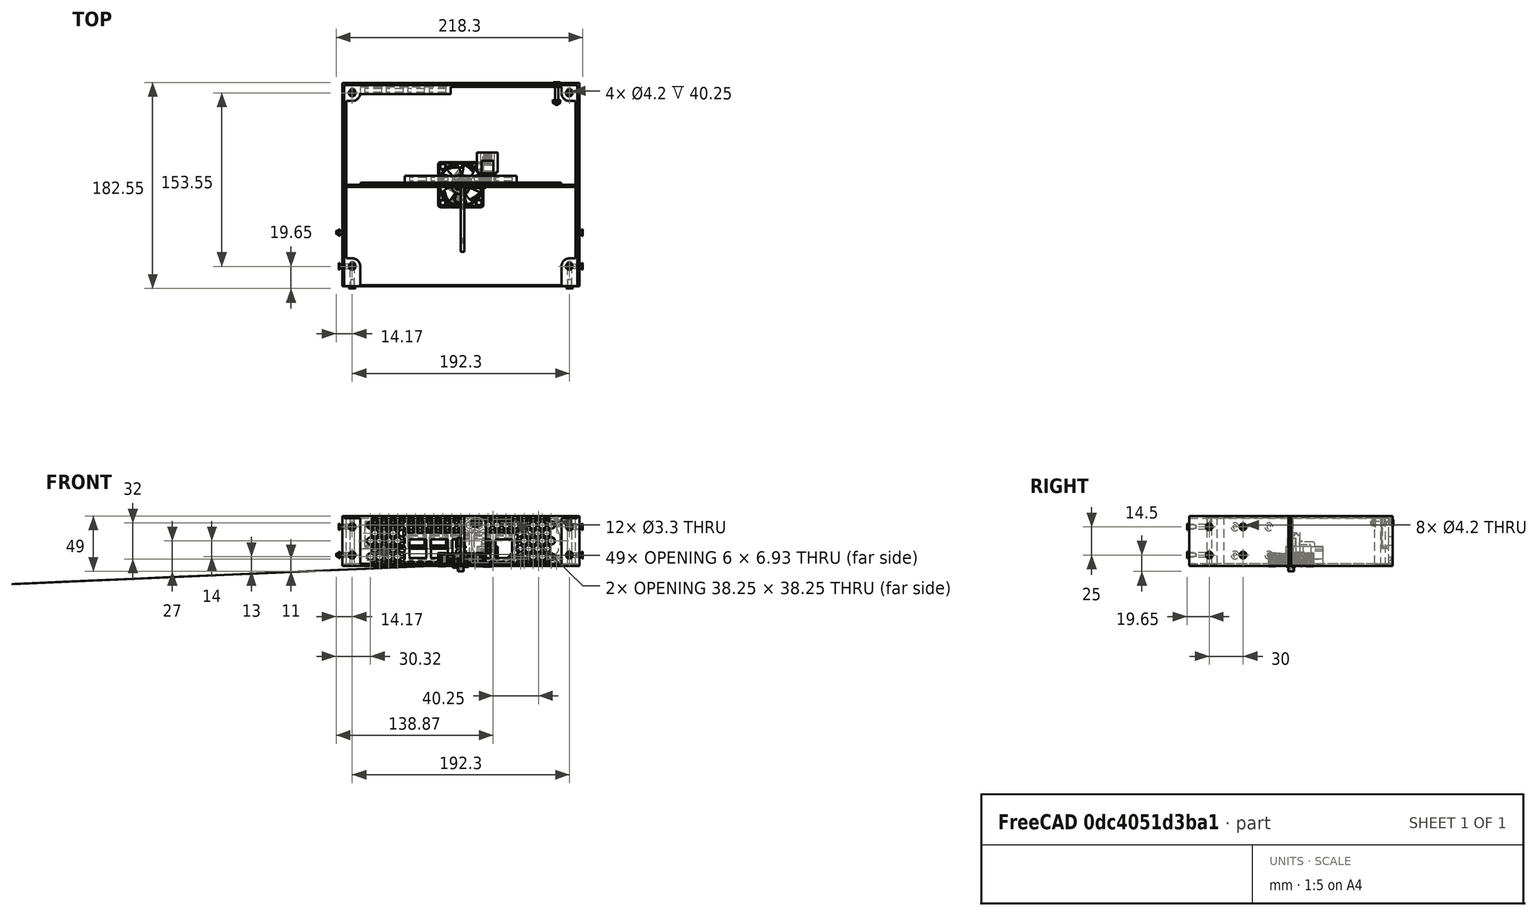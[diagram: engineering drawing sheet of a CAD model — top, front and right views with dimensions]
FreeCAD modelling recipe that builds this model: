
FCSTD DOCUMENT  (FreeCAD 1.1R20260108 (Git shallow))
Label: Rack box
License: All rights reserved
LicenseURL: https://en.wikipedia.org/wiki/All_rights_reserved
objects: Part::Feature×35, App::FeaturePython×25, Sketcher::SketchObject×22, Part::FeaturePython×19, App::Point×15, PartDesign::Pocket×12, PartDesign::Pad×10, App::Part×10, PartDesign::LinearPattern×7, PartDesign::Chamfer×6, App::Link×6, PartDesign::Body×4, PartDesign::MultiTransform×4, PartDesign::Mirrored×3, PartDesign::Fillet×2, Spreadsheet::Sheet×1, App::DocumentObjectGroup×1, PartDesign::Plane×1, Assembly::JointGroup×1, Assembly::AssemblyObject×1
note: 221 computed .brp shape members not serialized (recipe doc carries the construction recipe); baked Part::Feature solids carry a one-line shape summary decoded from their .brp

FEATURE [Spreadsheet::Sheet] Spreadsheet  label="Params"
  cells = A1='Box Length; B1(boxLength)=180; A2='Box Width; B2(boxWidth)=210; A3='Box Height; B3=1; C3='Constrained :; D3(boxHeight)==min(3; max(B3; 1)); A5='Rack ear depth; B5(rackEarDepth)=50; A6='Rack ear thickness; B6(rackEarThickness)=3; A7='Rack Unit; B7(rackUnit)=44.45; A8='Rack Unit Tolerance; B8(rackUnitTolerance)=0.45; A9='Rack Total Width; B9(rackTotalWidth)=254; A10='Rack Hole Spread; B10(rackHoleSpread)=236.525; A11='Rack Hole Spacing; B11(rackHoleSpacing)=15.875; C11='From center hole; A12='Rack hole Diameter; B12(rackHoleDiam)=6; A13='Wall Thickness; B13(wallThickness)=1.75; A14='Front thickness; B14(frontThickness)=2; A16='M3 heat set insert diam; B16(M3InsertDiam)=4.2; A17='Fit tolerance; B17(fitTol)=0.25; A18='M3 Screw hole; B18(M3ScrewHole)=3.3; A19='ISO 10642 Cone depth+tol; B19(iso10642coneDetph)=1.85; A20='Front Hole tp-bottom spacing; B20(frontHoleTopBottomSpace)=9.5; A22='Keystone Hole Width; B22(keystoneHoleWidth)=14.8; A23='Keystone Hole Height; B23(keystoneHoleHeight)=16.8; A24='Keystone Catch Height; B24(keystoneCatchHeight)=19.8; C24='From bottom of keystone; A25='Keystone Stop depth; B25(keystoneStopDepth)=9.75; A26='Keystone Catch Depth; B26(keystoneCatchDepth)=8.2; A27='Keystone Amount Front X; B27(keystoneFrontX)=5; A28='Keystone Amount Front Y; B28(keystoneFrontY)=1; A29='Keystone Amount Back X; B29(keystoneBackX)=4; A30='AndersonPowerpole Width; B30(andersonPowerpoleWidth)=16.75; A31='AndersonPowerpole Height; B31(andersonPowerpoleHeight)=8.75; A32='AndersonPowerpole Length; B32(andersonPowerpoleLength)=24.75; A35='Vent Hole Diam; B35(ventHoleDiam)=6; A36='Fan amount X; B36(fanAmountX)=2; C36='max 3; A37='Fan amout Y; B37(fanAmountY)=5; C37='max box height; A39='Rack Ear Thickness (3D printed); B39(rackEarThick3D)=3
FEATURE [App::DocumentObjectGroup] Measurements
FEATURE [Sketcher::SketchObject] Sketch011
  ArcFitTolerance = 1e-06
  AttachmentSupport = -> [YZ_Plane013]
  ExternalTypes = [0]
  FullyConstrained = true
  MakeInternals = false
  MapMode = 5
  Placement = pos=(0,0,0) rot=(0.57735,0.57735,0.57735;2.0944rad)
  expr: Constraints[14] = <<Params>>.M3ScrewHole
  expr: Constraints[28] = <<Params>>.boxHeight * <<Params>>.rackUnit - <<Params>>.rackUnitTolerance - 2 * <<Params>>.frontHoleTopBottomSpace
  expr: Constraints[30] = <<Params>>.frontThickness + 17.6
  expr: Constraints[32] = (<<Params>>.rackUnit * <<Params>>.boxHeight - <<Params>>.rackUnitTolerance) / 2
  expr: Constraints[33] = <<Params>>.rackUnit * <<Params>>.boxHeight - <<Params>>.rackUnitTolerance
  sketch-geometry (14):
    g0: LineSegment StartX=0 StartY=44 StartZ=0 EndX=-59.6 EndY=44 EndZ=0
    g1: LineSegment StartX=-59.6 StartY=44 StartZ=0 EndX=-59.6 EndY=0 EndZ=0
    g2: LineSegment StartX=-59.6 StartY=0 StartZ=0 EndX=0 EndY=0 EndZ=0
    g3: LineSegment StartX=0 StartY=0 StartZ=0 EndX=0 EndY=44 EndZ=0
    g4: LineSegment [constr] StartX=-49.6 StartY=9.5 StartZ=0 EndX=-49.6 EndY=0 EndZ=0
    g5: Circle CenterX=-49.6 CenterY=34.5 CenterZ=0 NormalX=0 NormalY=0 NormalZ=1 AngleXU=0 Radius=1.65
    g6: Circle CenterX=-19.6 CenterY=34.5 CenterZ=0 NormalX=0 NormalY=0 NormalZ=1 AngleXU=0 Radius=1.65
    g7: Circle CenterX=-49.6 CenterY=9.5 CenterZ=0 NormalX=0 NormalY=0 NormalZ=1 AngleXU=0 Radius=1.65
    g8: Circle CenterX=-19.6 CenterY=9.5 CenterZ=0 NormalX=0 NormalY=0 NormalZ=1 AngleXU=0 Radius=1.65
    g9: LineSegment [constr] StartX=-49.6 StartY=34.5 StartZ=0 EndX=-19.6 EndY=34.5 EndZ=0
    g10: LineSegment [constr] StartX=-19.6 StartY=34.5 StartZ=0 EndX=-19.6 EndY=9.5 EndZ=0
    g11: LineSegment [constr] StartX=-19.6 StartY=9.5 StartZ=0 EndX=-49.6 EndY=9.5 EndZ=0
    g12: LineSegment [constr] StartX=-49.6 StartY=9.5 StartZ=0 EndX=-49.6 EndY=34.5 EndZ=0
    g13: GeomPoint [constr] X=-19.6 Y=22 Z=0
  constraints (36):
    c: Coincident(g0,g1)
    c: Coincident(g1,g2)
    c: Coincident(g2,g3)
    c: Coincident(g3,g0)
    c: Horizontal(g0)
    c: Horizontal(g2)
    c: Vertical(g1)
    c: Vertical(g3)
    c: PointOnObject(g4,g2)
    c: Vertical(g4)
    c: Coincident(g7,g4)
    c: Equal(g7,g5)
    c: Equal(g5,g6)
    c: Equal(g6,g8)
    c: Diameter(g7) = 3.3
    c: Coincident(g9,g5)
    c: Coincident(g9,g6)
    c: Horizontal(g9)
    c: Coincident(g10,g6)
    c: Coincident(g10,g8)
    c: Vertical(g10)
    c: Coincident(g11,g8)
    c: Coincident(g11,g4)
    c: Horizontal(g11)
    c: Coincident(g12,g4)
    c: Coincident(g12,g5)
    c: Vertical(g12)
    c: DistanceX(g9,g9) = 30
    c: DistanceY(g10,g10) = 25
    c: PointOnObject(g-1,g2)
    c: DistanceX(g8,g2) = 19.6
    c: Symmetric(g10,g10,g13)
    c: DistanceY(g-1,g13) = 22
    c: DistanceY(g3,g3) = 44
    c: PointOnObject(g-1,g3)
    c: DistanceX(g1,g8) = 40
FEATURE [PartDesign::Pad] Pad006
  Direction = (1,0,0)
  Length = 3
  Length2 = 10
  Placement = pos=(0,0,0) rot=(1,1,1;2.0944rad)
  Profile = -> Sketch011
  ReferenceAxis = -> Sketch011 [N_Axis]
  Refine = true
  SideType = 0
  Suppressed = false
  Type = 0
  Type2 = 0
  expr: Length = <<Params>>.rackEarThick3D
FEATURE [PartDesign::Chamfer] Chamfer003
  Angle = 45
  Base = -> Pad006 [Edge15,Edge18,Edge21,Edge24]
  BaseFeature = -> Pad006
  ChamferType = 0
  FlipDirection = false
  Placement = pos=(0,0,0) rot=(1,1,1;2.0944rad)
  Refine = true
  Size = 1.85
  Size2 = 1
  SupportTransform = false
  Suppressed = false
  UseAllEdges = false
  expr: Size = min(<<Params>>.iso10642coneDetph; <<Params>>.rackEarThick3D - 0.01)
FEATURE [Sketcher::SketchObject] Sketch012
  ArcFitTolerance = 1e-06
  AttachmentSupport = -> [Chamfer003]
  ExternalGeometry = -> [Chamfer003]
  ExternalTypes = [0]
  FullyConstrained = true
  MakeInternals = false
  MapMode = 5
  Placement = pos=(3,-7e-16,3e-16) rot=(0.57735,0.57735,0.57735;2.0944rad)
  expr: Constraints[10] = <<Params>>.rackEarThick3D
  sketch-geometry (4):
    g0: LineSegment StartX=3.6e-15 StartY=44 StartZ=0 EndX=-3 EndY=44 EndZ=0
    g1: LineSegment StartX=-3 StartY=44 StartZ=0 EndX=-3 EndY=0 EndZ=0
    g2: LineSegment StartX=-3 StartY=0 StartZ=0 EndX=3.6e-15 EndY=0 EndZ=0
    g3: LineSegment StartX=3.6e-15 StartY=0 StartZ=0 EndX=3.6e-15 EndY=44 EndZ=0
  constraints (11):
    c: Coincident(g0,g1)
    c: Coincident(g1,g2)
    c: Coincident(g2,g3)
    c: Coincident(g3,g0)
    c: Horizontal(g0)
    c: Horizontal(g2)
    c: Vertical(g1)
    c: Vertical(g3)
    c: Coincident(g0,g-3)
    c: PointOnObject(g-3,g2)
    c: DistanceX(g0,g0) = 3
FEATURE [PartDesign::Pad] Pad007
  BaseFeature = -> Chamfer003
  Direction = (1,0,0)
  Length = 19
  Length2 = 10
  Placement = pos=(0,0,0) rot=(1,1,1;2.0944rad)
  Profile = -> Sketch012
  ReferenceAxis = -> Sketch012 [N_Axis]
  Refine = true
  SideType = 0
  Suppressed = false
  Type = 0
  Type2 = 0
  expr: Length = (<<Params>>.rackTotalWidth - <<Params>>.boxWidth) / 2 - <<Params>>.rackEarThick3D
FEATURE [Sketcher::SketchObject] Sketch
  ArcFitTolerance = 1e-06
  AttachmentSupport = -> [XY_Plane002]
  ExternalTypes = [0]
  FullyConstrained = true
  MakeInternals = false
  MapMode = 2
  expr: Constraints[10] = <<Params>>.boxWidth
  expr: Constraints[11] = <<Params>>.boxLength
  sketch-geometry (5):
    g0: LineSegment StartX=-105 StartY=90 StartZ=0 EndX=-105 EndY=-90 EndZ=0
    g1: LineSegment StartX=-105 StartY=-90 StartZ=0 EndX=105 EndY=-90 EndZ=0
    g2: LineSegment StartX=105 StartY=-90 StartZ=0 EndX=105 EndY=90 EndZ=0
    g3: LineSegment StartX=105 StartY=90 StartZ=0 EndX=-105 EndY=90 EndZ=0
    g4: GeomPoint [constr] X=2e-16 Y=-2e-16 Z=0
  constraints (12):
    c: Coincident(g0,g1)
    c: Coincident(g1,g2)
    c: Coincident(g2,g3)
    c: Coincident(g3,g0)
    c: Vertical(g0)
    c: Vertical(g2)
    c: Horizontal(g1)
    c: Horizontal(g3)
    c: Symmetric(g2,g0,g4)
    c: Coincident(g4,g-1)
    c: DistanceX(g3,g3) = 210
    c: DistanceY(g2,g2) = 180
FEATURE [PartDesign::Pad] Pad  label="PROBLEMATIC_PAD"
  Direction = (0,0,1)
  Length = 44
  Length2 = 10
  Profile = -> Sketch
  ReferenceAxis = -> Sketch [N_Axis]
  Refine = true
  SideType = 0
  Suppressed = false
  Type = 0
  Type2 = 0
  expr: Length = <<Params>>.boxHeight * <<Params>>.rackUnit - <<Params>>.rackUnitTolerance
FEATURE [Sketcher::SketchObject] Sketch001
  ArcFitTolerance = 1e-06
  AttachmentSupport = -> [Pad]
  ExternalTypes = [0]
  FullyConstrained = true
  MakeInternals = false
  MapMode = 5
  Placement = pos=(0,0,44) rot=(0,0,1;0rad)
  expr: Constraints[10] = <<Params>>.boxWidth - 2 * <<Params>>.wallThickness
  expr: Constraints[11] = <<Params>>.boxLength - <<Params>>.wallThickness
  expr: Constraints[12] = <<Params>>.boxLength / 2 - <<Params>>.wallThickness
  sketch-geometry (5):
    g0: LineSegment StartX=-103.25 StartY=-90 StartZ=0 EndX=103.25 EndY=-90 EndZ=0
    g1: LineSegment StartX=103.25 StartY=-90 StartZ=0 EndX=103.25 EndY=88.25 EndZ=0
    g2: LineSegment StartX=103.25 StartY=88.25 StartZ=0 EndX=-103.25 EndY=88.25 EndZ=0
    g3: LineSegment StartX=-103.25 StartY=88.25 StartZ=0 EndX=-103.25 EndY=-90 EndZ=0
    g4: GeomPoint X=0 Y=-90 Z=0
  constraints (13):
    c: Coincident(g0,g1)
    c: Coincident(g1,g2)
    c: Coincident(g2,g3)
    c: Coincident(g3,g0)
    c: Horizontal(g0)
    c: Horizontal(g2)
    c: Vertical(g1)
    c: Vertical(g3)
    c: Symmetric(g0,g0,g4)
    c: PointOnObject(g4,g-2)
    c: DistanceX(g2,g2) = 206.5
    c: DistanceY(g3,g3) = 178.25
    c: DistanceY(g-1,g2) = 88.25
FEATURE [PartDesign::Pocket] Pocket
  BaseFeature = -> Pad
  Direction = (0,0,-1)
  Length = 0
  Length2 = 5
  Offset = -1.75
  Profile = -> Sketch001
  ReferenceAxis = -> Sketch001 [N_Axis]
  Refine = true
  SideType = 0
  Suppressed = false
  Type = 3
  Type2 = 0
  UpToFace = -> Pad [Face5]
  expr: Offset = -<<Params>>.wallThickness
FEATURE [Sketcher::SketchObject] Sketch002
  ArcFitTolerance = 1e-06
  AttachmentSupport = -> [Pocket]
  ExternalTypes = [0]
  FullyConstrained = true
  MakeInternals = false
  MapMode = 5
  Placement = pos=(0,0,1.75) rot=(0,0,1;0rad)
  expr: Constraints[0] = <<Params>>.M3InsertDiam
  expr: Constraints[23] = <<Params>>.boxWidth / 2 - <<Params>>.wallThickness
  expr: Constraints[25] = 17.6 mm
  expr: Constraints[26] = <<Params>>.boxLength / 2
  expr: Constraints[31] = <<Params>>.boxLength - <<Params>>.wallThickness
  expr: Constraints[36] = <<Params>>.wallThickness
  expr: Constraints[65] = <<Params>>.wallThickness
  sketch-geometry (27):
    g0: Circle CenterX=-96.15 CenterY=81.15 CenterZ=0 NormalX=0 NormalY=0 NormalZ=1 AngleXU=0 Radius=2.1
    g1: LineSegment StartX=-89.05 StartY=-90 StartZ=0 EndX=-89.05 EndY=-72.4 EndZ=0
    g2: Circle CenterX=-96.15 CenterY=-72.4 CenterZ=0 NormalX=0 NormalY=0 NormalZ=1 AngleXU=0 Radius=2.1
    g3: ArcOfCircle CenterX=-96.15 CenterY=81.15 CenterZ=0 NormalX=0 NormalY=0 NormalZ=1 AngleXU=0 Radius=7.1 StartAngle=4.71239 EndAngle=6.28319
    g4: ArcOfCircle CenterX=-96.15 CenterY=-72.4 CenterZ=0 NormalX=0 NormalY=0 NormalZ=1 AngleXU=0 Radius=7.1 StartAngle=2e-16 EndAngle=1.5708
    g5: LineSegment [constr] StartX=-96.15 StartY=81.15 StartZ=0 EndX=-96.15 EndY=-72.4 EndZ=0
    g6: LineSegment StartX=-89.05 StartY=-90 StartZ=0 EndX=-103.25 EndY=-90 EndZ=0
    g7: LineSegment StartX=-101.5 StartY=74.05 StartZ=0 EndX=-101.5 EndY=-65.3 EndZ=0
    g8: LineSegment StartX=-96.15 StartY=74.05 StartZ=0 EndX=-101.5 EndY=74.05 EndZ=0
    g9: LineSegment StartX=-101.5 StartY=-65.3 StartZ=0 EndX=-96.15 EndY=-65.3 EndZ=0
    g10: LineSegment StartX=-103.25 StartY=-90 StartZ=0 EndX=-103.25 EndY=88.25 EndZ=0
    g11: LineSegment StartX=-89.05 StartY=86.5 StartZ=0 EndX=0 EndY=86.5 EndZ=0
    g12: LineSegment StartX=-89.05 StartY=81.15 StartZ=0 EndX=-89.05 EndY=86.5 EndZ=0
    g13: LineSegment StartX=-103.25 StartY=88.25 StartZ=0 EndX=0 EndY=88.25 EndZ=0
    g14: LineSegment StartX=103.25 StartY=88.25 StartZ=0 EndX=0 EndY=88.25 EndZ=0
    g15: LineSegment StartX=89.05 StartY=86.5 StartZ=0 EndX=0 EndY=86.5 EndZ=0
    g16: LineSegment StartX=89.05 StartY=81.15 StartZ=0 EndX=89.05 EndY=86.5 EndZ=0
    g17: ArcOfCircle CenterX=96.15 CenterY=81.15 CenterZ=0 NormalX=0 NormalY=0 NormalZ=1 AngleXU=0 Radius=7.1 StartAngle=3.14159 EndAngle=4.71239
    g18: LineSegment StartX=96.15 StartY=74.05 StartZ=0 EndX=101.5 EndY=74.05 EndZ=0
    g19: LineSegment StartX=103.25 StartY=-90 StartZ=0 EndX=103.25 EndY=88.25 EndZ=0
    g20: Circle CenterX=96.15 CenterY=81.15 CenterZ=0 NormalX=0 NormalY=0 NormalZ=1 AngleXU=0 Radius=2.1
    g21: ArcOfCircle CenterX=96.15 CenterY=-72.4 CenterZ=0 NormalX=0 NormalY=0 NormalZ=1 AngleXU=0 Radius=7.1 StartAngle=1.5708 EndAngle=3.14159
    g22: LineSegment StartX=89.05 StartY=-90 StartZ=0 EndX=89.05 EndY=-72.4 EndZ=0
    g23: LineSegment StartX=89.05 StartY=-90 StartZ=0 EndX=103.25 EndY=-90 EndZ=0
    g24: LineSegment StartX=101.5 StartY=-65.3 StartZ=0 EndX=96.15 EndY=-65.3 EndZ=0
    g25: LineSegment StartX=101.5 StartY=74.05 StartZ=0 EndX=101.5 EndY=-65.3 EndZ=0
    g26: Circle CenterX=96.15 CenterY=-72.4 CenterZ=0 NormalX=0 NormalY=0 NormalZ=1 AngleXU=0 Radius=2.1
  constraints (66):
    c: Diameter(g0) = 4.2
    c: Vertical(g1)
    c: Equal(g0,g2)
    c: Coincident(g3,g0)
    c: Coincident(g4,g2)
    c: Tangent(g4,g1) = -1.5708
    c: Coincident(g5,g0)
    c: Coincident(g5,g2)
    c: Vertical(g5)
    c: Distance(g2,g1) = 5
    c: Coincident(g6,g1)
    c: Vertical(g7)
    c: Coincident(g8,g7)
    c: Horizontal(g8)
    c: Tangent(g8,g3) = 1.5708
    c: Coincident(g9,g7)
    c: Horizontal(g9)
    c: Tangent(g9,g4) = 1.5708
    c: Coincident(g10,g6)
    c: Distance(g0,g10) = 5
    c: Distance(g3,g0) = 5
    c: Horizontal(g11)
    c: Coincident(g12,g11)
    c: DistanceX(g6,g-1) = 103.25
    c: Vertical(g10)
    c: DistanceY(g6,g2) = 17.6
    c: DistanceY(g6,g-1) = 90
    c: Horizontal(g6)
    c: PointOnObject(g11,g-2)
    c: Tangent(g12,g3) = -1.5708
    c: Vertical(g12)
    c: DistanceY(g10,g10) = 178.25
    c: Equal(g8,g12)
    c: Coincident(g13,g10)
    c: PointOnObject(g13,g-2)
    c: Horizontal(g13)
    c: Distance(g11,g13) = 1.75
    c: Equal(g0,g20)
    c: Symmetric(g0,g20,g-2)
    c: Symmetric(g1,g22,g-2)
    c: Symmetric(g1,g22,g-2)
    c: Equal(g3,g17)
    c: Symmetric(g3,g17,g-2)
    c: Symmetric(g3,g17,g-2)
    c: Equal(g4,g21)
    c: Symmetric(g4,g21,g-2)
    c: Symmetric(g4,g21,g-2)
    c: Symmetric(g6,g23,g-2)
    c: Symmetric(g6,g23,g-2)
    c: Symmetric(g7,g25,g-2)
    c: Symmetric(g7,g25,g-2)
    c: Symmetric(g8,g18,g-2)
    c: Symmetric(g8,g18,g-2)
    c: Symmetric(g9,g24,g-2)
    c: Symmetric(g9,g24,g-2)
    c: Symmetric(g10,g19,g-2)
    c: Symmetric(g10,g19,g-2)
    c: Symmetric(g11,g15,g-2)
    c: Symmetric(g12,g16,g-2)
    c: Symmetric(g12,g16,g-2)
    c: Symmetric(g13,g14,g-2)
    c: Coincident(g15,g11)
    c: Coincident(g14,g13)
    c: Equal(g2,g26)
    c: Symmetric(g2,g26,g-2)
    c: DistanceX(g10,g7) = 1.75
FEATURE [PartDesign::Pad] Pad001
  BaseFeature = -> Pocket
  Direction = (0,0,1)
  Length = 10
  Length2 = 10
  Offset = 2
  Profile = -> Sketch002
  ReferenceAxis = -> Sketch002 [N_Axis]
  Refine = true
  SideType = 0
  Suppressed = false
  Type = 3
  Type2 = 0
  UpToFace = -> Pocket [Face5]
  expr: Offset = <<Params>>.wallThickness + <<Params>>.fitTol
FEATURE [Sketcher::SketchObject] Sketch003
  ArcFitTolerance = 1e-06
  AttachmentSupport = -> [Pad001]
  ExternalTypes = [0]
  FullyConstrained = true
  MakeInternals = false
  MapMode = 5
  Placement = pos=(0,-90,0) rot=(1,0,0;1.5708rad)
  expr: .Constraints.frontHole = <<Params>>.M3InsertDiam
  expr: Constraints[10] = <<Params>>.rackUnit * <<Params>>.boxHeight - <<Params>>.rackUnitTolerance
  expr: Constraints[11] = <<Params>>.boxWidth / 2 - (<<Params>>.wallThickness + 5 + <<Params>>.M3InsertDiam / 2)
  expr: Constraints[9] = <<Params>>.boxHeight * <<Params>>.rackUnit - <<Params>>.rackUnitTolerance - 2 * <<Params>>.frontHoleTopBottomSpace
  sketch-geometry (9):
    g0: LineSegment [constr] StartX=-96.15 StartY=44 StartZ=0 EndX=-96.15 EndY=0 EndZ=0
    g1: GeomPoint [constr] X=-96.15 Y=22 Z=0
    g2: Circle CenterX=-96.15 CenterY=34.5 CenterZ=0 NormalX=0 NormalY=0 NormalZ=1 AngleXU=0 Radius=2.1
    g3: Circle CenterX=-96.15 CenterY=9.5 CenterZ=0 NormalX=0 NormalY=0 NormalZ=1 AngleXU=0 Radius=2.1
    g4: Circle CenterX=96.15 CenterY=34.5 CenterZ=0 NormalX=0 NormalY=0 NormalZ=1 AngleXU=0 Radius=2.1
    g5: Circle CenterX=96.15 CenterY=9.5 CenterZ=0 NormalX=0 NormalY=0 NormalZ=1 AngleXU=0 Radius=2.1
    g6: LineSegment [constr] StartX=-96.15 StartY=0 StartZ=0 EndX=0 EndY=0 EndZ=0
    g7: LineSegment [constr] StartX=-96.15 StartY=34.5 StartZ=0 EndX=-96.15 EndY=9.5 EndZ=0
    g8: GeomPoint [constr] X=-96.15 Y=22 Z=0
  constraints (19):
    c: Vertical(g0)
    c: Symmetric(g0,g0,g1)
    c: PointOnObject(g2,g0)
    c: Diameter(g2) = 4.2  'frontHole'
    c: Equal(g3,g2)
    c: Equal(g2,g4)
    c: Symmetric(g2,g4,g-2)
    c: Equal(g3,g5)
    c: Symmetric(g3,g5,g-2)
    c: DistanceY(g3,g2) = 25
    c: DistanceY(g-1,g0) = 44
    c: DistanceX(g0,g-1) = 96.15
    c: Coincident(g6,g0)
    c: Coincident(g6,g-1)
    c: Horizontal(g6)
    c: Coincident(g7,g2)
    c: Coincident(g7,g3)
    c: Symmetric(g7,g7,g8)
    c: Coincident(g8,g1)
FEATURE [PartDesign::Pocket] Pocket001
  BaseFeature = -> Pad001
  Direction = (0,1,-2e-16)
  Length = 17.6
  Length2 = 5
  Offset = 2.1
  Profile = -> Sketch003
  ReferenceAxis = -> Sketch003 [N_Axis]
  Refine = true
  SideType = 0
  Suppressed = false
  Type = 0
  Type2 = 0
  UpToShape = -> [Pad001]
  expr: Length = 17.6
  expr: Offset = <<Params>>.M3InsertDiam / 2
FEATURE [Sketcher::SketchObject] Sketch010
  ArcFitTolerance = 1e-06
  AttachmentSupport = -> [Pocket001]
  ExternalTypes = [0]
  FullyConstrained = true
  MakeInternals = false
  MapMode = 5
  Placement = pos=(-105,0,0) rot=(0.57735,-0.57735,-0.57735;2.0944rad)
  expr: Constraints[15] = <<Params>>.M3InsertDiam
  expr: Constraints[17] = <<Params>>.rackUnit * <<Params>>.boxHeight - <<Params>>.rackUnitTolerance - 2 * <<Params>>.frontHoleTopBottomSpace
  expr: Constraints[20] = (<<Params>>.rackUnit * <<Params>>.boxHeight - <<Params>>.rackUnitTolerance) / 2
  expr: Constraints[21] = <<Params>>.boxLength / 2 - 17.6
  sketch-geometry (9):
    g0: LineSegment [constr] StartX=72.4 StartY=34.5 StartZ=0 EndX=42.4 EndY=34.5 EndZ=0
    g1: LineSegment [constr] StartX=42.4 StartY=34.5 StartZ=0 EndX=42.4 EndY=9.5 EndZ=0
    g2: LineSegment [constr] StartX=42.4 StartY=9.5 StartZ=0 EndX=72.4 EndY=9.5 EndZ=0
    g3: LineSegment [constr] StartX=72.4 StartY=9.5 StartZ=0 EndX=72.4 EndY=34.5 EndZ=0
    g4: Circle CenterX=42.4 CenterY=9.5 CenterZ=0 NormalX=0 NormalY=0 NormalZ=1 AngleXU=0 Radius=2.1
    g5: Circle CenterX=72.4 CenterY=9.5 CenterZ=0 NormalX=0 NormalY=0 NormalZ=1 AngleXU=0 Radius=2.1
    g6: Circle CenterX=42.4 CenterY=34.5 CenterZ=0 NormalX=0 NormalY=0 NormalZ=1 AngleXU=0 Radius=2.1
    g7: Circle CenterX=72.4 CenterY=34.5 CenterZ=0 NormalX=0 NormalY=0 NormalZ=1 AngleXU=0 Radius=2.1
    g8: GeomPoint [constr] X=72.4 Y=22 Z=0
  constraints (22):
    c: Coincident(g0,g1)
    c: Coincident(g1,g2)
    c: Coincident(g2,g3)
    c: Coincident(g3,g0)
    c: Horizontal(g0)
    c: Horizontal(g2)
    c: Vertical(g1)
    c: Vertical(g3)
    c: PointOnObject(g5,g2)
    c: DistanceX(g2,g2) = 30
    c: Coincident(g4,g1)
    c: Coincident(g6,g0)
    c: Equal(g7,g6)
    c: Equal(g6,g4)
    c: Equal(g4,g5)
    c: Diameter(g4) = 4.2
    c: Coincident(g0,g7)
    c: DistanceY(g1,g1) = 25
    c: PointOnObject(g5,g3)
    c: Symmetric(g3,g3,g8)
    c: DistanceY(g-1,g8) = 22
    c: DistanceX(g-1,g5) = 72.4
FEATURE [PartDesign::Pocket] Pocket004
  BaseFeature = -> Pocket001
  Direction = (1,0,0)
  Length = 0
  Length2 = 5
  Offset = 7.1
  Profile = -> Sketch010
  ReferenceAxis = -> Sketch010 [N_Axis]
  Refine = true
  SideType = 0
  Suppressed = false
  Type = 3
  Type2 = 0
  UpToFace = -> Pocket001 [Face3]
  expr: Offset = <<Params>>.M3InsertDiam / 2 + 5
FEATURE [PartDesign::Mirrored] Mirrored002
  BaseFeature = -> Pocket004
  MirrorPlane = -> YZ_Plane002
  Originals = -> [Pocket004]
  Refine = true
  Suppressed = false
  TransformMode = 0
FEATURE [Sketcher::SketchObject] Sketch013
  ArcFitTolerance = 1e-06
  AttachmentSupport = -> [Pad007]
  ExternalTypes = [0]
  FullyConstrained = true
  MakeInternals = false
  MapMode = 5
  Placement = pos=(0,3e-16,0) rot=(0.57735,0.57735,0.57735;4.18879rad)
  expr: Constraints[0] = <<Params>>.rackHoleDiam
  expr: Constraints[18] = <<Params>>.rackHoleDiam / 2 + <<Params>>.fitTol
  expr: Constraints[1] = <<Params>>.boxHeight > 1 ? <<Params>>.rackUnit * <<Params>>.boxHeight - (<<Params>>.rackUnit - <<Params>>.rackUnitTolerance) : <<Params>>.rackHoleSpacing * 2
  expr: Constraints[6] = <<Params>>.boxHeight > 1 ? <<Params>>.rackUnit / 2 - <<Params>>.rackUnitTolerance / 2 : <<Params>>.rackUnit / 2 - <<Params>>.rackUnitTolerance / 2 - <<Params>>.rackHoleSpacing
  expr: Constraints[7] = (<<Params>>.rackHoleSpread - <<Params>>.boxWidth) / 2
  sketch-geometry (13):
    g0: Circle [constr] CenterX=37.875 CenterY=13.2625 CenterZ=0 NormalX=0 NormalY=0 NormalZ=1 AngleXU=0 Radius=3
    g1: LineSegment [constr] StartX=37.875 StartY=13.2625 StartZ=0 EndX=6.125 EndY=13.2625 EndZ=0
    g2: Circle [constr] CenterX=6.125 CenterY=13.2625 CenterZ=0 NormalX=0 NormalY=0 NormalZ=1 AngleXU=0 Radius=3
    g3: ArcOfCircle CenterX=6.125 CenterY=14.7625 CenterZ=0 NormalX=0 NormalY=0 NormalZ=1 AngleXU=0 Radius=3.25 StartAngle=2e-16 EndAngle=3.14159
    g4: ArcOfCircle CenterX=6.125 CenterY=11.7625 CenterZ=0 NormalX=0 NormalY=0 NormalZ=1 AngleXU=0 Radius=3.25 StartAngle=3.14159 EndAngle=6.28319
    g5: LineSegment StartX=9.375 StartY=14.7625 StartZ=0 EndX=9.375 EndY=11.7625 EndZ=0
    g6: LineSegment StartX=2.875 StartY=14.7625 StartZ=0 EndX=2.875 EndY=11.7625 EndZ=0
    g7: LineSegment [constr] StartX=6.125 StartY=14.7625 StartZ=0 EndX=6.125 EndY=11.7625 EndZ=0
    g8: ArcOfCircle CenterX=37.875 CenterY=14.7625 CenterZ=0 NormalX=0 NormalY=0 NormalZ=1 AngleXU=0 Radius=3.25 StartAngle=2e-16 EndAngle=3.14159
    g9: ArcOfCircle CenterX=37.875 CenterY=11.7625 CenterZ=0 NormalX=0 NormalY=0 NormalZ=1 AngleXU=0 Radius=3.25 StartAngle=3.14159 EndAngle=6.28319
    g10: LineSegment StartX=41.125 StartY=14.7625 StartZ=0 EndX=41.125 EndY=11.7625 EndZ=0
    g11: LineSegment StartX=34.625 StartY=14.7625 StartZ=0 EndX=34.625 EndY=11.7625 EndZ=0
    g12: LineSegment [constr] StartX=37.875 StartY=14.7625 StartZ=0 EndX=37.875 EndY=11.7625 EndZ=0
  constraints (30):
    c: Diameter(g0) = 6
    c: Distance(g1,g1) = 31.75
    c: Coincident(g2,g1)
    c: Equal(g2,g0)
    c: Coincident(g1,g0)
    c: Horizontal(g1)
    c: DistanceX(g-1,g1) = 6.125
    c: Distance(g1,g-1) = 13.2625
    c: Tangent(g3,g5) = 1.5708
    c: Tangent(g3,g6) = -1.5708
    c: Tangent(g4,g5) = 1.5708
    c: Tangent(g4,g6) = -1.5708
    c: Equal(g3,g4)
    c: Coincident(g7,g3)
    c: Coincident(g7,g4)
    c: Symmetric(g7,g7,g1)
    c: Vertical(g7)
    c: DistanceY(g4,g3) = 3
    c: Radius(g3) = 3.25
    c: Tangent(g8,g10) = 1.5708
    c: Tangent(g8,g11) = -1.5708
    c: Tangent(g9,g10) = 1.5708
    c: Tangent(g9,g11) = -1.5708
    c: Equal(g8,g9)
    c: Coincident(g12,g8)
    c: Coincident(g12,g9)
    c: Symmetric(g12,g12,g0)
    c: Vertical(g12)
    c: Equal(g8,g3)
    c: Equal(g5,g11)
FEATURE [PartDesign::Pocket] Pocket005
  BaseFeature = -> Pad007
  Direction = (0,-1,0)
  Length = 5
  Length2 = 5
  Placement = pos=(0,0,0) rot=(1,1,1;2.0944rad)
  Profile = -> Sketch013
  ReferenceAxis = -> Sketch013 [N_Axis]
  Refine = true
  SideType = 0
  Suppressed = false
  Type = 1
  Type2 = 0
FEATURE [PartDesign::Fillet] Fillet
  Base = -> Pocket005 [Edge13]
  BaseFeature = -> Pocket005
  Placement = pos=(0,0,0) rot=(1,1,1;2.0944rad)
  Radius = 1.5
  Refine = true
  SupportTransform = false
  Suppressed = false
  UseAllEdges = false
FEATURE [Sketcher::SketchObject] Sketch014
  ArcFitTolerance = 1e-06
  AttachmentSupport = -> [Pocket001]
  ExternalTypes = [0]
  FullyConstrained = true
  MakeInternals = false
  MapMode = 5
  Placement = pos=(0,86.5,0) rot=(1,0,0;1.5708rad)
  expr: Constraints[19] = <<Params>>.M3ScrewHole
  expr: Constraints[20] = 39 / 2
  expr: Constraints[56] = (<<Params>>.rackUnit * <<Params>>.boxHeight - <<Params>>.rackUnitTolerance) / 2 - 32 / 2 - (min(<<Params>>.boxHeight; <<Params>>.fanAmountY) - 1) * (40 + <<Params>>.fitTol) / 2
  expr: Constraints[57] = <<Params>>.boxWidth / 2 - (<<Params>>.wallThickness + 5 + <<Params>>.M3InsertDiam + 5) - <<Params>>.fitTol
  sketch-geometry (22):
    g0: LineSegment [constr] StartX=52.8 StartY=6 StartZ=0 EndX=84.8 EndY=6 EndZ=0
    g1: LineSegment [constr] StartX=84.8 StartY=6 StartZ=0 EndX=84.8 EndY=38 EndZ=0
    g2: LineSegment [constr] StartX=84.8 StartY=38 StartZ=0 EndX=52.8 EndY=38 EndZ=0
    g3: LineSegment [constr] StartX=52.8 StartY=38 StartZ=0 EndX=52.8 EndY=6 EndZ=0
    g4: Circle CenterX=52.8 CenterY=38 CenterZ=0 NormalX=0 NormalY=0 NormalZ=1 AngleXU=0 Radius=1.65
    g5: Circle CenterX=84.8 CenterY=38 CenterZ=0 NormalX=0 NormalY=0 NormalZ=1 AngleXU=0 Radius=1.65
    g6: Circle CenterX=52.8 CenterY=6 CenterZ=0 NormalX=0 NormalY=0 NormalZ=1 AngleXU=0 Radius=1.65
    g7: Circle CenterX=84.8 CenterY=6 CenterZ=0 NormalX=0 NormalY=0 NormalZ=1 AngleXU=0 Radius=1.65
    g8: LineSegment [constr] StartX=84.8 StartY=6 StartZ=0 EndX=52.8 EndY=38 EndZ=0
    g9: ArcOfCircle CenterX=68.8 CenterY=22 CenterZ=0 NormalX=0 NormalY=0 NormalZ=1 AngleXU=0 Radius=19.5 StartAngle=0.196432 EndAngle=1.37436
    g10: ArcOfCircle CenterX=68.8 CenterY=22 CenterZ=0 NormalX=0 NormalY=0 NormalZ=1 AngleXU=0 Radius=19.5 StartAngle=1.76723 EndAngle=2.94516
    g11: ArcOfCircle CenterX=68.8 CenterY=22 CenterZ=0 NormalX=0 NormalY=0 NormalZ=1 AngleXU=0 Radius=19.5 StartAngle=3.33802 EndAngle=4.51596
    g12: ArcOfCircle CenterX=68.8 CenterY=22 CenterZ=0 NormalX=0 NormalY=0 NormalZ=1 AngleXU=0 Radius=19.5 StartAngle=4.90882 EndAngle=6.08675
    g13: LineSegment StartX=49.675 StartY=25.8058 StartZ=0 EndX=49.675 EndY=18.1942 EndZ=0
    g14: LineSegment StartX=64.9942 StartY=2.875 StartZ=0 EndX=72.6058 EndY=2.875 EndZ=0
    g15: LineSegment StartX=87.925 StartY=18.1942 StartZ=0 EndX=87.925 EndY=25.8058 EndZ=0
    g16: LineSegment StartX=72.6058 StartY=41.125 StartZ=0 EndX=64.9942 EndY=41.125 EndZ=0
    g17: LineSegment [constr] StartX=48.8 StartY=2 StartZ=0 EndX=88.8 EndY=2 EndZ=0
    g18: LineSegment [constr] StartX=88.8 StartY=2 StartZ=0 EndX=88.8 EndY=42 EndZ=0
    g19: LineSegment [constr] StartX=88.8 StartY=42 StartZ=0 EndX=48.8 EndY=42 EndZ=0
    g20: LineSegment [constr] StartX=48.8 StartY=42 StartZ=0 EndX=48.8 EndY=2 EndZ=0
    g21: GeomPoint [constr] X=68.8 Y=22 Z=0
  constraints (58):
    c: Coincident(g0,g1)
    c: Coincident(g1,g2)
    c: Coincident(g2,g3)
    c: Coincident(g3,g0)
    c: Horizontal(g0)
    c: Horizontal(g2)
    c: Vertical(g1)
    c: Vertical(g3)
    c: Equal(g2,g3)
    c: DistanceX(g2,g2) = 32
    c: Coincident(g4,g2)
    c: Coincident(g5,g1)
    c: Coincident(g6,g0)
    c: Coincident(g7,g0)
    c: Coincident(g8,g0)
    c: Coincident(g8,g2)
    c: Equal(g4,g5)
    c: Equal(g5,g7)
    c: Equal(g7,g6)
    c: Diameter(g4) = 3.3
    c: Radius(g9) = 19.5
    c: Symmetric(g8,g8,g9)
    c: Coincident(g10,g9)
    c: Coincident(g11,g9)
    c: Coincident(g12,g9)
    c: Equal(g12,g10)
    c: Equal(g10,g11)
    c: Equal(g11,g9)
    c: Coincident(g13,g10)
    c: Coincident(g13,g11)
    c: Coincident(g14,g11)
    c: Coincident(g14,g12)
    c: Coincident(g15,g12)
    c: Coincident(g15,g9)
    c: Coincident(g16,g9)
    c: Coincident(g16,g10)
    c: Equal(g16,g14)
    c: Equal(g14,g13)
    c: Equal(g13,g15)
    c: Horizontal(g16)
    c: Horizontal(g14)
    c: Vertical(g13)
    c: Vertical(g15)
    c: Coincident(g17,g18)
    c: Coincident(g18,g19)
    c: Coincident(g19,g20)
    c: Coincident(g20,g17)
    c: Horizontal(g17)
    c: Horizontal(g19)
    c: Vertical(g18)
    c: Vertical(g20)
    c: Symmetric(g19,g17,g21)
    c: Distance(g18,g20) = 40
    c: Distance(g17,g19) = 40
    c: Symmetric(g8,g8,g21)
    c: Distance(g19,g16) = 0.875
    c: DistanceY(g-1,g0) = 6
    c: DistanceX(g-1,g17) = 88.8
FEATURE [Part::Feature] Part__Feature  label="Case"
  shape: bbox 53.93 x 53.93 x 11.4 mm, 549 faces (baked)
FEATURE [Part::Feature] Part__Feature001  label="Silent block"
  Placement = pos=(-16,16,10) rot=(0,0,1;0rad)
  shape: bbox 6.6 x 6.6 x 1.4 mm, 11 faces (baked)
FEATURE [Part::Feature] Part__Feature002  label="Silent block001"
  Placement = pos=(16,16,10) rot=(0,0,-1;1.5708rad)
  shape: bbox 6.6 x 6.6 x 1.4 mm, 11 faces (baked)
FEATURE [Part::Feature] Part__Feature003  label="Silent block002"
  Placement = pos=(16,-16,10) rot=(0,0,1;3.14159rad)
  shape: bbox 6.6 x 6.6 x 1.4 mm, 11 faces (baked)
FEATURE [Part::Feature] Part__Feature004  label="Silent block003"
  Placement = pos=(-16,-16,10) rot=(0,0,1;1.5708rad)
  shape: bbox 6.6 x 6.6 x 1.4 mm, 11 faces (baked)
FEATURE [Part::Feature] Part__Feature005  label="Silent block004"
  Placement = pos=(-16,16,-0.4) rot=(0,0,1;0rad)
  shape: bbox 6.6 x 6.6 x 1.4 mm, 11 faces (baked)
FEATURE [Part::Feature] Part__Feature006  label="Silent block005"
  Placement = pos=(16,16,-0.4) rot=(0,0,-1;1.5708rad)
  shape: bbox 6.6 x 6.6 x 1.4 mm, 11 faces (baked)
FEATURE [Part::Feature] Part__Feature007  label="Silent block006"
  Placement = pos=(16,-16,-0.4) rot=(0,0,1;3.14159rad)
  shape: bbox 6.6 x 6.6 x 1.4 mm, 11 faces (baked)
FEATURE [Part::Feature] Part__Feature008  label="Silent block007"
  Placement = pos=(-16,-16,-0.4) rot=(0,0,1;1.5708rad)
  shape: bbox 6.6 x 6.6 x 1.4 mm, 11 faces (baked)
FEATURE [Part::Feature] Part__Feature009  label="Magnet"
  Placement = pos=(0,0,0.4) rot=(0,0,1;0rad)
  shape: bbox 4.08 x 4.08 x 0.9 mm, 4 faces (baked)
FEATURE [Part::Feature] Part__Feature010  label="Back plate"
  shape: bbox 15.2 x 15.2 x 0.4 mm, 4 faces (baked)
FEATURE [Part::Feature] Part__Feature011  label="Impeller"
  Placement = pos=(-3e-16,-1e-15,10.2) rot=(0,0,-1;1.33658rad)
  shape: bbox 36.14 x 36.09 x 6.5 mm, 209 faces (baked)
FEATURE [Part::Feature] Part__Feature012  label="Magnetic screen"
  Placement = pos=(-3e-16,-1e-15,3.7) rot=(0,0,-1;1.14696rad)
  shape: bbox 16.85 x 16.85 x 6 mm, 6 faces (baked)
FEATURE [Part::Feature] Part__Feature013  label="Rotor"
  Placement = pos=(4e-16,-3e-15,3.7) rot=(0.645942,0.763387,0;3.14159rad)
  shape: bbox 17.56 x 17.56 x 6.1 mm, 7 faces (baked)
FEATURE [Part::Feature] Part__Feature014  label="Shaft"
  Placement = pos=(-3e-16,-1e-15,9.8) rot=(0,0,-1;1.40451rad)
  shape: bbox 2.066 x 2.066 x 7.506 mm, 190 faces (baked)
FEATURE [Part::Feature] Part__Feature015  label="Bearing"
  shape: bbox 5 x 5 x 5 mm, 15 faces (baked)
FEATURE [Part::Feature] Part__Feature016  label="Bearing gasket"
  Placement = pos=(0,0,-1.3) rot=(0,0,1;0rad)
  shape: bbox 2 x 2 x 0.5 mm, 6 faces (baked)
FEATURE [Part::Feature] Part__Feature017  label="Oil"
  Placement = pos=(0,0,-4.5) rot=(0,0,1;0rad)
  shape: bbox 4 x 4 x 2.7 mm, 6 faces (baked)
FEATURE [Part::Feature] Part__Feature018  label="Bearing gasket001"
  Placement = pos=(0,0,-4.5) rot=(0,0,1;0rad)
  shape: bbox 2 x 2 x 0.5 mm, 6 faces (baked)
FEATURE [App::Part] Oil_Bearing  label="Oil Bearing"
  Group = -> [Part__Feature015,Part__Feature016,Part__Feature017,Part__Feature018]
  Origin = -> Origin015
  Placement = pos=(0,-1.4e-14,2) rot=(1,0,0;3.14159rad)
FEATURE [Part::Feature] Part__Feature019  label="Board"
  shape: bbox 16 x 16 x 0.8 mm, 18 faces (baked)
FEATURE [Part::Feature] Part__Feature020  label="Stator"
  Placement = pos=(0,0,3.55) rot=(0,0,1;0rad)
  shape: bbox 11.93 x 12 x 5.5 mm, 2869 faces, 97 solids (baked)
FEATURE [Part::Feature] Part__Feature021  label="Hall Effect sensor_WE"
  Placement = pos=(-5.3023,-0.939061,0) rot=(0.486876,0.617637,-0.617637;4.04778rad)
  shape: bbox 3.532 x 6.423 x 1.6 mm, 105 faces, 4 solids (baked)
FEATURE [Part::Feature] Part__Feature022  label="Controller"
  Placement = pos=(5.15743,2.31948,4e-16) rot=(-0.701528,0.503914,-0.503914;1.91809rad)
  shape: bbox 4.252 x 5.458 x 1.013 mm, 445 faces, 13 solids (baked)
FEATURE [Part::Feature] Part__Feature023  label="Coil"
  Placement = pos=(1e-16,-5.01,1.29) rot=(0,0.707107,0.707107;3.14159rad)
  shape: bbox 2.411 x 1.581 x 5.411 mm, 116 faces (baked)
FEATURE [Part::Feature] Part__Feature024  label="Coil001"
  Placement = pos=(-4.33879,-2.505,1.29) rot=(0.377964,0.654654,0.654654;2.41886rad)
  shape: bbox 2.506 x 2.704 x 5.411 mm, 116 faces (baked)
FEATURE [Part::Feature] Part__Feature025  label="Coil002"
  Placement = pos=(-4.33879,2.505,1.29) rot=(0.774597,0.447214,0.447214;1.82348rad)
  shape: bbox 2.327 x 2.801 x 5.411 mm, 116 faces (baked)
FEATURE [Part::Feature] Part__Feature026  label="Coil003"
  Placement = pos=(3.49e-14,5.01,1.29) rot=(1,0,0;1.5708rad)
  shape: bbox 2.411 x 1.581 x 5.411 mm, 116 faces (baked)
FEATURE [Part::Feature] Part__Feature027  label="Coil004"
  Placement = pos=(4.33879,2.505,1.29) rot=(0.774597,-0.447214,-0.447214;1.82348rad)
  shape: bbox 2.506 x 2.704 x 5.411 mm, 116 faces (baked)
FEATURE [Part::Feature] Part__Feature028  label="Coil005"
  Placement = pos=(4.33879,-2.505,1.29) rot=(-0.377964,0.654654,0.654654;3.86433rad)
  shape: bbox 2.327 x 2.801 x 5.411 mm, 116 faces (baked)
FEATURE [Part::Feature] Part__Feature029  label="Pieza2^Brushless motor"
  shape: bbox 10.82 x 13.16 x 6.905 mm, 136 faces, 7 solids (baked)
FEATURE [Part::Feature] Part__Feature030  label="Pieza3^Brushless motor"
  Placement = pos=(0,0,0.8) rot=(0,0,1;0rad)
  shape: bbox 4.1 x 0.7354 x 1.7 mm, 22 faces, 3 solids (baked)
FEATURE [App::Part] Brushless_motor  label="Brushless motor"
  Group = -> [Part__Feature019,Part__Feature020,Part__Feature021,Part__Feature022,Part__Feature023,Part__Feature024,Part__Feature025,Part__Feature026,Part__Feature027,Part__Feature028,Part__Feature029,Part__Feature030]
  Origin = -> Origin016
  Placement = pos=(0,1.526e-13,2) rot=(0,0,1;0rad)
FEATURE [Part::Feature] Part__Feature031  label="Wires^NF-A4x10 FLX"
  Placement = pos=(0,0,2) rot=(0,1,0;3.14159rad)
  shape: bbox 13.87 x 12.88 x 7.684 mm, 145 faces, 6 solids (baked)
FEATURE [App::Part] NF_A4x10_FLX  label="NF-A4x10 FLX"
  Group = -> [Part__Feature,Part__Feature001,Part__Feature002,Part__Feature003,Part__Feature004,Part__Feature005,Part__Feature006,Part__Feature007,Part__Feature008,Part__Feature009,Part__Feature010,Part__Feature011,Part__Feature012,Part__Feature013,Part__Feature014,Oil_Bearing,Brushless_motor,Part__Feature031]
  Origin = -> Origin017
  Placement = pos=(60.25,86.1,21.875) rot=(0,-0.707107,0.707107;3.14159rad)
FEATURE [Sketcher::SketchObject] Sketch016  label="CoverPlateSketch"
  ArcFitTolerance = 1e-06
  AttachmentSupport = -> [XZ_Plane018]
  ExternalTypes = [0]
  FullyConstrained = true
  MakeInternals = false
  MapMode = 5
  Placement = pos=(0,0,0) rot=(1,0,0;1.5708rad)
  expr: Constraints[11] = <<Params>>.boxHeight * <<Params>>.rackUnit - <<Params>>.rackUnitTolerance
  expr: Constraints[12] = <<Params>>.boxWidth
  expr: Constraints[15] = <<Params>>.rackUnit * <<Params>>.boxHeight - <<Params>>.rackUnitTolerance - 2 * <<Params>>.frontHoleTopBottomSpace
  expr: Constraints[1] = <<Params>>.M3ScrewHole
  expr: Constraints[20] = (<<Params>>.boxHeight * <<Params>>.rackUnit - <<Params>>.rackUnitTolerance) / 2
  expr: Constraints[21] = <<Params>>.M3InsertDiam / 2 + 5 + <<Params>>.wallThickness
  sketch-geometry (11):
    g0: Circle CenterX=-96.15 CenterY=34.5 CenterZ=0 NormalX=0 NormalY=0 NormalZ=1 AngleXU=0 Radius=1.65
    g1: Circle CenterX=-96.15 CenterY=9.5 CenterZ=0 NormalX=0 NormalY=0 NormalZ=1 AngleXU=0 Radius=1.65
    g2: LineSegment StartX=-105 StartY=44 StartZ=0 EndX=-105 EndY=0 EndZ=0
    g3: LineSegment StartX=-105 StartY=0 StartZ=0 EndX=105 EndY=0 EndZ=0
    g4: LineSegment StartX=105 StartY=0 StartZ=0 EndX=105 EndY=44 EndZ=0
    g5: LineSegment StartX=105 StartY=44 StartZ=0 EndX=-105 EndY=44 EndZ=0
    g6: GeomPoint [constr] X=0 Y=0 Z=0
    g7: LineSegment [constr] StartX=-96.15 StartY=34.5 StartZ=0 EndX=-96.15 EndY=9.5 EndZ=0
    g8: GeomPoint [constr] X=-96.15 Y=22 Z=0
    g9: Circle CenterX=96.15 CenterY=34.5 CenterZ=0 NormalX=0 NormalY=0 NormalZ=1 AngleXU=0 Radius=1.65
    g10: Circle CenterX=96.15 CenterY=9.5 CenterZ=0 NormalX=0 NormalY=0 NormalZ=1 AngleXU=0 Radius=1.65
  constraints (26):
    c: Equal(g0,g1)
    c: Diameter(g0) = 3.3
    c: Coincident(g2,g3)
    c: Coincident(g3,g4)
    c: Coincident(g4,g5)
    c: Coincident(g5,g2)
    c: Vertical(g2)
    c: Vertical(g4)
    c: Horizontal(g3)
    c: Horizontal(g5)
    c: PointOnObject(g3,g-1)
    c: DistanceY(g2,g2) = 44
    c: DistanceX(g3,g3) = 210
    c: Symmetric(g3,g3,g6)
    c: PointOnObject(g6,g-2)
    c: DistanceY(g1,g0) = 25
    c: Coincident(g7,g0)
    c: Coincident(g7,g1)
    c: Vertical(g7)
    c: Symmetric(g7,g7,g8)
    c: DistanceY(g-1,g8) = 22
    c: DistanceX(g2,g1) = 8.85
    c: Equal(g0,g9)
    c: Symmetric(g0,g9,g-2)
    c: Equal(g1,g10)
    c: Symmetric(g1,g10,g-2)
FEATURE [PartDesign::Pad] Pad009  label="CoverPlatePad"
  Direction = (0,-1,2e-16)
  Length = 2
  Length2 = 10
  Placement = pos=(0,0,0) rot=(1,0,0;1.5708rad)
  Profile = -> Sketch016
  ReferenceAxis = -> Sketch016 [N_Axis]
  Refine = true
  SideType = 0
  Suppressed = false
  Type = 0
  Type2 = 0
  expr: Length = <<Params>>.frontThickness
FEATURE [PartDesign::Chamfer] Chamfer004  label="ISO10642"
  Angle = 45
  Base = -> Pad009 [Edge21,Edge24,Edge18,Edge15]
  BaseFeature = -> Pad009
  ChamferType = 0
  FlipDirection = false
  Placement = pos=(0,0,0) rot=(1,0,0;1.5708rad)
  Refine = true
  Size = 1.85
  Size2 = 1
  SupportTransform = false
  Suppressed = false
  UseAllEdges = false
  expr: Size = min(<<Params>>.iso10642coneDetph; <<Params>>.frontThickness - 0.01)
FEATURE [PartDesign::Plane] DatumPlane001  label="VentHoleMidSymmetry"
  AttachmentOffset = pos=(0,0,-22) rot=(0,0,1;0rad)
  AttachmentSupport = -> [Pad009]
  Length = 230.494
  MapMode = 5
  Placement = pos=(0,0,22) rot=(1,0,0;3.14159rad)
  ResizeMode = 0
  Width = 70.4939
  expr: .AttachmentOffset.Base.z = -(<<Params>>.boxHeight * <<Params>>.rackUnit - <<Params>>.rackUnitTolerance) / 2
FEATURE [PartDesign::Mirrored] Mirrored004
  MirrorPlane = -> DatumPlane001
  Placement = pos=(0,0,0) rot=(1,0,0;1.5708rad)
  Refine = true
  Suppressed = false
  TransformMode = 0
FEATURE [Sketcher::SketchObject] Sketch017  label="VentHoleSketch"
  ArcFitTolerance = 1e-06
  AttachmentSupport = -> [Chamfer004]
  ExternalTypes = [0]
  FullyConstrained = true
  MakeInternals = false
  MapMode = 5
  Placement = pos=(0,4.9e-15,0) rot=(-1,0,0;1.5708rad)
  expr: Constraints[18] = <<Params>>.ventHoleDiam
  expr: Constraints[20] = (<<Params>>.rackUnit * <<Params>>.boxHeight - <<Params>>.rackUnitTolerance) / 2
  sketch-geometry (16):
    g0: LineSegment StartX=-3 StartY=-20.2679 StartZ=0 EndX=-3 EndY=-23.7321 EndZ=0
    g1: LineSegment StartX=-3 StartY=-23.7321 StartZ=0 EndX=6.688e-13 EndY=-25.4641 EndZ=0
    g2: LineSegment StartX=6.688e-13 StartY=-25.4641 StartZ=0 EndX=3 EndY=-23.7321 EndZ=0
    g3: LineSegment StartX=3 StartY=-23.7321 StartZ=0 EndX=3 EndY=-20.2679 EndZ=0
    g4: LineSegment StartX=3 StartY=-20.2679 StartZ=0 EndX=-1.8745e-12 EndY=-18.5359 EndZ=0
    g5: LineSegment StartX=-1.8747e-12 StartY=-18.5359 StartZ=0 EndX=-3 EndY=-20.2679 EndZ=0
    g6: Circle [constr] CenterX=-2.914e-13 CenterY=-22 CenterZ=0 NormalX=0 NormalY=0 NormalZ=1 AngleXU=0 Radius=3.4641
    g7: LineSegment StartX=-1 StartY=-16.8038 StartZ=0 EndX=-1 EndY=-13.3397 EndZ=0
    g8: LineSegment StartX=-1 StartY=-13.3397 StartZ=0 EndX=-4 EndY=-11.6077 EndZ=0
    g9: LineSegment StartX=-4 StartY=-11.6077 StartZ=0 EndX=-7 EndY=-13.3397 EndZ=0
    g10: LineSegment StartX=-7 StartY=-13.3397 StartZ=0 EndX=-7 EndY=-16.8038 EndZ=0
    g11: LineSegment StartX=-7 StartY=-16.8038 StartZ=0 EndX=-4 EndY=-18.5359 EndZ=0
    g12: LineSegment StartX=-4 StartY=-18.5359 StartZ=0 EndX=-1 EndY=-16.8038 EndZ=0
    g13: Circle [constr] CenterX=-4 CenterY=-15.0718 CenterZ=0 NormalX=0 NormalY=0 NormalZ=1 AngleXU=0 Radius=3.4641
    g14: LineSegment [constr] StartX=-4 StartY=-18.5359 StartZ=0 EndX=-1.8749e-12 EndY=-18.5359 EndZ=0
    g15: LineSegment [constr] StartX=-1 StartY=-16.8038 StartZ=0 EndX=-1.8747e-12 EndY=-18.5359 EndZ=0
  constraints (38):
    c: Coincident(g0,g1)
    c: Coincident(g1,g2)
    c: Coincident(g2,g3)
    c: Coincident(g3,g4)
    c: Coincident(g4,g5)
    c: Coincident(g5,g0)
    c: Equal(g0, g1-g5) x5
    c: PointOnObject(g0,g6)
    c: PointOnObject(g1,g6)
    c: PointOnObject(g2,g6)
    c: PointOnObject(g3,g6)
    c: PointOnObject(g4,g6)
    c: PointOnObject(g5,g6)
    c: PointOnObject(g6,g-2)
    c: Distance(g2,g0) = 6
    c: Vertical(g0)
    c: DistanceY(g6,g-1) = 22
    c: Coincident(g7,g8)
    c: Coincident(g8,g9)
    c: Coincident(g9,g10)
    c: Coincident(g10,g11)
    c: Coincident(g11,g12)
    c: Coincident(g12,g7)
    c: Equal(g7, g8-g12) x5
    c: PointOnObject(g7,g13)
    c: PointOnObject(g8,g13)
    c: PointOnObject(g9,g13)
    c: PointOnObject(g10,g13)
    c: PointOnObject(g11,g13)
    c: PointOnObject(g12,g13)
    c: Equal(g7,g3)
    c: Parallel(g7,g3)
    c: Coincident(g14,g11)
    c: Coincident(g14,g4)
    c: Horizontal(g14)
    c: Coincident(g15,g7)
    c: Coincident(g15,g4)
    c: Perpendicular(g12,g15)
FEATURE [PartDesign::LinearPattern] LinearPattern005
  Direction = -> Sketch017 [H_Axis]
  Length = 80
  Length2 = 100
  Mode = 1
  Mode2 = 0
  Occurrences = 11
  Occurrences2 = 1
  Offset = 8
  Offset2 = 10
  Placement = pos=(0,0,0) rot=(1,0,0;1.5708rad)
  Refine = true
  Reversed2 = false
  SpacingPattern = [0]
  SpacingPattern2 = [0]
  Spacings = [-1,-1,-1,-1,-1,-1,-1,-1,-1,-1]
  Suppressed = false
  TransformMode = 0
  expr: Occurrences = (<<Params>>.boxWidth / 2 - <<Params>>.wallThickness - 15) / (<<Params>>.ventHoleDiam * 4 / 3)
  expr: Offset = <<Params>>.ventHoleDiam * 4 / 3
FEATURE [PartDesign::LinearPattern] LinearPattern006
  Direction = -> Sketch017 [V_Axis]
  Length = 14
  Length2 = 100
  Mode = 1
  Mode2 = 0
  Occurrences = 2
  Occurrences2 = 1
  Offset = 14
  Offset2 = 10
  Placement = pos=(0,0,0) rot=(1,0,0;1.5708rad)
  Refine = true
  Reversed2 = false
  SpacingPattern = [0]
  SpacingPattern2 = [0]
  Spacings = [-1]
  Suppressed = false
  TransformMode = 0
  expr: Occurrences = max(round(<<Params>>.rackUnit * <<Params>>.boxHeight - 2 * <<Params>>.wallThickness) / (<<Params>>.ventHoleDiam * 4 * cos(30)) - 1; 2)
  expr: Offset = <<Params>>.ventHoleDiam * (2 * 3 + 1) / 3
FEATURE [PartDesign::Mirrored] Mirrored003
  MirrorPlane = -> Sketch017 [V_Axis]
  Placement = pos=(0,0,0) rot=(1,0,0;1.5708rad)
  Refine = true
  Suppressed = false
  TransformMode = 0
FEATURE [Sketcher::SketchObject] Sketch019  label="KeystoneHolderSlab"
  ArcFitTolerance = 1e-06
  AttachmentSupport = -> [Chamfer004]
  ExternalTypes = [0]
  FullyConstrained = true
  MakeInternals = false
  MapMode = 5
  Placement = pos=(0,-2,0) rot=(1,0,0;1.5708rad)
  expr: Constraints[10] = <<Params>>.wallThickness + 2
  expr: Constraints[11] = min(4.2 + (4.2 + <<Params>>.keystoneHoleWidth) * <<Params>>.keystoneFrontX; <<Params>>.boxWidth - 2 * (<<Params>>.wallThickness * 2 + 10 + <<Params>>.M3InsertDiam))
  expr: Constraints[12] = min(<<Params>>.boxHeight * <<Params>>.rackUnit - <<Params>>.rackUnitTolerance - 4 * <<Params>>.wallThickness; 3 + min(<<Params>>.keystoneFrontY; <<Params>>.boxHeight) * (<<Params>>.keystoneCatchHeight + 3) + (<<Params>>.keystoneFrontY - 1) * 1)
  sketch-geometry (5):
    g0: LineSegment StartX=-49.6 StartY=29.55 StartZ=0 EndX=-49.6 EndY=3.75 EndZ=0
    g1: LineSegment StartX=-49.6 StartY=3.75 StartZ=0 EndX=49.6 EndY=3.75 EndZ=0
    g2: LineSegment StartX=49.6 StartY=3.75 StartZ=0 EndX=49.6 EndY=29.55 EndZ=0
    g3: LineSegment StartX=49.6 StartY=29.55 StartZ=0 EndX=-49.6 EndY=29.55 EndZ=0
    g4: GeomPoint X=0 Y=3.75 Z=0
  constraints (13):
    c: Coincident(g0,g1)
    c: Coincident(g1,g2)
    c: Coincident(g2,g3)
    c: Coincident(g3,g0)
    c: Vertical(g0)
    c: Vertical(g2)
    c: Horizontal(g1)
    c: Horizontal(g3)
    c: Symmetric(g1,g1,g4)
    c: PointOnObject(g4,g-2)
    c: DistanceY(g-1,g4) = 3.75
    c: Distance(g3,g3) = 99.2
    c: DistanceY(g2,g2) = 25.8
FEATURE [Part::Feature] Part__Feature032  label="Keystone  RJ45"
  Placement = pos=(30.7273,-9,26.9137) rot=(-0.57735,-0.57735,0.57735;2.0944rad)
  shape: bbox 18.55 x 27.94 x 22.83 mm, 233 faces (baked)
FEATURE [App::Part] _Sin_guardar_  label="RJ45 Keystone"
  Group = -> [Part__Feature032]
  Origin = -> Origin022
FEATURE [PartDesign::Pocket] Pocket006  label="fanHole"
  BaseFeature = -> Mirrored002
  Direction = (0,1,-2e-16)
  Length = 5
  Length2 = 5
  Profile = -> Sketch014
  ReferenceAxis = -> Sketch014 [N_Axis]
  Refine = true
  SideType = 0
  Suppressed = false
  Type = 1
  Type2 = 0
FEATURE [PartDesign::LinearPattern] LinearPattern003
  Direction = -> Sketch014 [H_Axis]
  Length = 40.25
  Length2 = 100
  Mode = 1
  Mode2 = 0
  Occurrences = 2
  Occurrences2 = 1
  Offset = 40.25
  Offset2 = 10
  Refine = true
  Reversed = true
  Reversed2 = false
  SpacingPattern = [0]
  SpacingPattern2 = [0]
  Spacings = [-1]
  Suppressed = false
  TransformMode = 0
  expr: Occurrences = min(3; <<Params>>.fanAmountX)
  expr: Offset = 40 + <<Params>>.fitTol
FEATURE [PartDesign::LinearPattern] LinearPattern004
  Direction = -> Sketch014 [V_Axis]
  Length = 40.25
  Length2 = 100
  Mode = 1
  Mode2 = 0
  Occurrences = 1
  Occurrences2 = 1
  Offset = 40.25
  Offset2 = 10
  Refine = true
  Reversed2 = false
  SpacingPattern = [0]
  SpacingPattern2 = [0]
  Spacings2 = [0]
  Suppressed = false
  TransformMode = 0
  expr: Occurrences = min(<<Params>>.boxHeight; <<Params>>.fanAmountY)
  expr: Offset = 40 + <<Params>>.fitTol
FEATURE [PartDesign::LinearPattern] LinearPattern013
  Direction = -> X_Axis019
  Length = 76
  Length2 = 100
  Mode = 1
  Mode2 = 0
  Occurrences = 5
  Occurrences2 = 1
  Offset = 19
  Offset2 = 10
  Placement = pos=(0,0,0) rot=(1,0,0;1.5708rad)
  Refine = true
  Reversed2 = false
  SpacingPattern = [0]
  SpacingPattern2 = [0]
  Spacings = [-1,-1,-1,-1]
  Suppressed = false
  TransformMode = 0
  expr: Occurrences = <<Params>>.keystoneFrontX
  expr: Offset = <<Params>>.keystoneHoleWidth + 4.2
FEATURE [PartDesign::LinearPattern] LinearPattern014
  Direction = -> Z_Axis019
  Length = 25.8
  Length2 = 100
  Mode = 1
  Mode2 = 0
  Occurrences = 1
  Occurrences2 = 1
  Offset = 25.8
  Offset2 = 10
  Placement = pos=(0,0,0) rot=(1,0,0;1.5708rad)
  Refine = true
  Reversed2 = false
  SpacingPattern = [0]
  SpacingPattern2 = [0]
  Spacings2 = [0]
  Suppressed = false
  TransformMode = 0
  expr: Occurrences = <<Params>>.keystoneFrontY
  expr: Offset = <<Params>>.keystoneCatchHeight + 3 + 3
FEATURE [Sketcher::SketchObject] Sketch030  label="KeystoneSlab"
  ArcFitTolerance = 1e-06
  AttachmentSupport = -> [Mirrored002]
  ExternalTypes = [0]
  FullyConstrained = true
  MakeInternals = false
  MapMode = 5
  Placement = pos=(0,90,0) rot=(0,0.707107,0.707107;3.14159rad)
  expr: Constraints[10] = 4.2 + (<<Params>>.keystoneHoleWidth + 4.2) * <<Params>>.keystoneBackX
  expr: Constraints[11] = <<Params>>.rackUnit - <<Params>>.rackUnitTolerance - <<Params>>.wallThickness - <<Params>>.fitTol
  expr: Constraints[8] = <<Params>>.boxWidth / 2 - (<<Params>>.wallThickness + 5 + <<Params>>.M3InsertDiam + 5)
  expr: Constraints[9] = 3 + <<Params>>.keystoneCatchHeight + 4
  sketch-geometry (4):
    g0: LineSegment StartX=89.05 StartY=42 StartZ=0 EndX=8.85 EndY=42 EndZ=0
    g1: LineSegment StartX=8.85 StartY=42 StartZ=0 EndX=8.85 EndY=15.2 EndZ=0
    g2: LineSegment StartX=8.85 StartY=15.2 StartZ=0 EndX=89.05 EndY=15.2 EndZ=0
    g3: LineSegment StartX=89.05 StartY=15.2 StartZ=0 EndX=89.05 EndY=42 EndZ=0
  constraints (12):
    c: Coincident(g0,g1)
    c: Coincident(g1,g2)
    c: Coincident(g2,g3)
    c: Coincident(g3,g0)
    c: Horizontal(g0)
    c: Horizontal(g2)
    c: Vertical(g1)
    c: Vertical(g3)
    c: DistanceX(g-1,g2) = 89.05
    c: DistanceY(g3,g3) = 26.8
    c: DistanceX(g2,g2) = 80.2
    c: DistanceY(g-1,g0) = 42
FEATURE [Sketcher::SketchObject] Sketch031
  ArcFitTolerance = 1e-06
  AttachmentSupport = -> [XY_Plane024]
  ExternalTypes = [0]
  FullyConstrained = true
  MakeInternals = false
  MapMode = 5
  expr: Constraints[37] = 5 + <<Params>>.M3InsertDiam / 2 - <<Params>>.fitTol / 2
  expr: Constraints[38] = 17.6 - <<Params>>.fitTol / 2
  expr: Constraints[39] = 5 + <<Params>>.M3InsertDiam / 2
  expr: Constraints[6] = <<Params>>.boxWidth - <<Params>>.wallThickness * 2 - <<Params>>.fitTol
  expr: Constraints[7] = <<Params>>.boxLength - <<Params>>.wallThickness - <<Params>>.fitTol
  expr: Constraints[9] = <<Params>>.M3ScrewHole
  sketch-geometry (18):
    g0: LineSegment StartX=-103.125 StartY=88 StartZ=0 EndX=-103.125 EndY=-88 EndZ=0
    g1: LineSegment StartX=-102.125 StartY=-89 StartZ=0 EndX=102.125 EndY=-89 EndZ=0
    g2: LineSegment StartX=103.125 StartY=-88 StartZ=0 EndX=103.125 EndY=88 EndZ=0
    g3: LineSegment StartX=102.125 StartY=89 StartZ=0 EndX=-102.125 EndY=89 EndZ=0
    g4: GeomPoint [constr] X=0 Y=0 Z=0
    g5: Circle CenterX=-96.025 CenterY=82.025 CenterZ=0 NormalX=0 NormalY=0 NormalZ=1 AngleXU=0 Radius=1.65
    g6: Circle CenterX=-96.025 CenterY=-71.525 CenterZ=0 NormalX=0 NormalY=0 NormalZ=1 AngleXU=0 Radius=1.65
    g7: Circle CenterX=96.025 CenterY=82.025 CenterZ=0 NormalX=0 NormalY=0 NormalZ=1 AngleXU=0 Radius=1.65
    g8: Circle CenterX=96.025 CenterY=-71.525 CenterZ=0 NormalX=0 NormalY=0 NormalZ=1 AngleXU=0 Radius=1.65
    g9: ArcOfCircle CenterX=-102.125 CenterY=88 CenterZ=0 NormalX=0 NormalY=0 NormalZ=1 AngleXU=0 Radius=1 StartAngle=1.5708 EndAngle=3.14159
    g10: GeomPoint [constr] X=-103.125 Y=89 Z=0
    g11: ArcOfCircle CenterX=-102.125 CenterY=-88 CenterZ=0 NormalX=0 NormalY=0 NormalZ=1 AngleXU=0 Radius=1 StartAngle=3.14159 EndAngle=4.71239
    g12: GeomPoint [constr] X=-103.125 Y=-89 Z=0
    g13: ArcOfCircle CenterX=102.125 CenterY=-88 CenterZ=0 NormalX=0 NormalY=0 NormalZ=1 AngleXU=0 Radius=1 StartAngle=4.71239 EndAngle=6.28319
    g14: GeomPoint [constr] X=103.125 Y=-89 Z=0
    g15: ArcOfCircle CenterX=102.125 CenterY=88 CenterZ=0 NormalX=0 NormalY=0 NormalZ=1 AngleXU=0 Radius=1 StartAngle=1.7e-15 EndAngle=1.5708
    g16: GeomPoint [constr] X=103.125 Y=89 Z=0
    g17: LineSegment [constr] StartX=-96.025 StartY=-71.525 StartZ=0 EndX=-96.025 EndY=82.025 EndZ=0
  constraints (40):
    c: Vertical(g0)
    c: Vertical(g2)
    c: Horizontal(g1)
    c: Horizontal(g3)
    c: Symmetric(g14,g10,g4)
    c: Coincident(g4,g-1)
    c: DistanceX(g10,g16) = 206.25
    c: DistanceY(g14,g16) = 178
    c: Equal(g6,g5)
    c: Diameter(g5) = 3.3
    c: Equal(g5,g7)
    c: Symmetric(g5,g7,g-2)
    c: Equal(g6,g8)
    c: Symmetric(g6,g8,g-2)
    c: PointOnObject(g10,g3)
    c: PointOnObject(g10,g0)
    c: Tangent(g3,g9) = -1.5708
    c: Tangent(g0,g9) = -1.5708
    c: PointOnObject(g12,g0)
    c: PointOnObject(g12,g1)
    c: Tangent(g0,g11) = -1.5708
    c: Tangent(g1,g11) = -1.5708
    c: PointOnObject(g14,g1)
    c: PointOnObject(g14,g2)
    c: Tangent(g1,g13) = -1.5708
    c: Tangent(g2,g13) = -1.5708
    c: PointOnObject(g16,g2)
    c: PointOnObject(g16,g3)
    c: Tangent(g2,g15) = -1.5708
    c: Tangent(g3,g15) = -1.5708
    c: Equal(g15,g9)
    c: Equal(g9,g11)
    c: Equal(g11,g13)
    c: Radius(g9) = 1
    c: Coincident(g17,g6)
    c: Coincident(g17,g5)
    c: Vertical(g17)
    c: Distance(g5,g3) = 6.975
    c: DistanceY(g12,g6) = 17.475
    c: Distance(g0,g17) = 7.1
FEATURE [PartDesign::Pad] Pad013
  Direction = (0,0,1)
  Length = 1.75
  Length2 = 10
  Profile = -> Sketch031
  ReferenceAxis = -> Sketch031 [N_Axis]
  Refine = true
  SideType = 0
  Suppressed = false
  Type = 0
  Type2 = 0
  expr: Length = <<Params>>.wallThickness
FEATURE [PartDesign::Chamfer] Chamfer
  Angle = 45
  Base = -> Pad013 [Edge27,Edge33,Edge30,Edge36]
  BaseFeature = -> Pad013
  ChamferType = 0
  FlipDirection = false
  Refine = true
  Size = 1.74
  Size2 = 1
  SupportTransform = false
  Suppressed = false
  UseAllEdges = false
  expr: Size = min(<<Params>>.wallThickness - 0.01; <<Params>>.iso10642coneDetph)
FEATURE [PartDesign::Body] Body006  label="topCover"
  AllowCompound = false
  Group = -> [Sketch031,Pad013,Chamfer]
  Origin = -> Origin024
  Tip = -> Chamfer
FEATURE [App::Part] Part007  label="Top Cover"
  Group = -> [Body006]
  Origin = -> Origin023
  Placement = pos=(-2e-16,-0.875,86.45) rot=(0,0,1;0rad)
FEATURE [Sketcher::SketchObject] Sketch032  label="KeystoneHoleSketch"
  ArcFitTolerance = 1e-06
  AttachmentSupport = -> [Pad]
  ExternalTypes = [0]
  FullyConstrained = true
  MakeInternals = false
  MapMode = 5
  Placement = pos=(0,90,0) rot=(0,0.707107,0.707107;3.14159rad)
  expr: Constraints[10] = <<Params>>.boxWidth / 2 - (<<Params>>.wallThickness + 5 + <<Params>>.M3InsertDiam + 5) - 4.2
  expr: Constraints[11] = <<Params>>.rackUnit - <<Params>>.rackUnitTolerance - <<Params>>.wallThickness - <<Params>>.keystoneCatchHeight - 4.2 - <<Params>>.fitTol
  expr: Constraints[8] = <<Params>>.keystoneHoleWidth
  expr: Constraints[9] = <<Params>>.keystoneHoleHeight
  sketch-geometry (4):
    g0: LineSegment StartX=70.05 StartY=34.8 StartZ=0 EndX=70.05 EndY=18 EndZ=0
    g1: LineSegment StartX=70.05 StartY=18 StartZ=0 EndX=84.85 EndY=18 EndZ=0
    g2: LineSegment StartX=84.85 StartY=18 StartZ=0 EndX=84.85 EndY=34.8 EndZ=0
    g3: LineSegment StartX=84.85 StartY=34.8 StartZ=0 EndX=70.05 EndY=34.8 EndZ=0
  constraints (12):
    c: Coincident(g0,g1)
    c: Coincident(g1,g2)
    c: Coincident(g2,g3)
    c: Coincident(g3,g0)
    c: Vertical(g0)
    c: Vertical(g2)
    c: Horizontal(g1)
    c: Horizontal(g3)
    c: DistanceX(g3,g3) = 14.8
    c: DistanceY(g2,g2) = 16.8
    c: DistanceX(g-1,g1) = 84.85
    c: DistanceY(g-1,g1) = 18
FEATURE [App::Link] Box  label="Box001"
  LinkedObject = -> Part
FEATURE [App::FeaturePython] GroundedJoint  # Assembly grounded joint (typed FeaturePython)
  ObjectToGround = -> Box
FEATURE [Sketcher::SketchObject] Sketch034  label="CatchHolesSketchBack"
  ArcFitTolerance = 1e-06
  AttachmentSupport = -> [Mirrored002]
  ExternalTypes = [0]
  FullyConstrained = true
  MakeInternals = false
  MapMode = 5
  Placement = pos=(-89.05,0,0) rot=(0.57735,0.57735,0.57735;2.0944rad)
  expr: Constraints[21] = <<Params>>.keystoneCatchHeight
  expr: Constraints[22] = <<Params>>.rackUnit - <<Params>>.rackUnitTolerance - <<Params>>.wallThickness - <<Params>>.keystoneCatchHeight - 4.2 - <<Params>>.fitTol
  expr: Constraints[23] = <<Params>>.boxLength / 2 - <<Params>>.keystoneCatchDepth
  sketch-geometry (8):
    g0: LineSegment StartX=81.8 StartY=18 StartZ=0 EndX=81.8 EndY=16.5 EndZ=0
    g1: LineSegment StartX=81.8 StartY=16.5 StartZ=0 EndX=84.8 EndY=16.5 EndZ=0
    g2: LineSegment StartX=84.8 StartY=16.5 StartZ=0 EndX=84.8 EndY=18 EndZ=0
    g3: LineSegment StartX=84.8 StartY=18 StartZ=0 EndX=81.8 EndY=18 EndZ=0
    g4: LineSegment StartX=87.8 StartY=39.3 StartZ=0 EndX=87.8 EndY=37.8 EndZ=0
    g5: LineSegment StartX=87.8 StartY=37.8 StartZ=0 EndX=84.8 EndY=37.8 EndZ=0
    g6: LineSegment StartX=84.8 StartY=37.8 StartZ=0 EndX=84.8 EndY=39.3 EndZ=0
    g7: LineSegment StartX=84.8 StartY=39.3 StartZ=0 EndX=87.8 EndY=39.3 EndZ=0
  constraints (24):
    c: Coincident(g0,g1)
    c: Coincident(g1,g2)
    c: Coincident(g2,g3)
    c: Coincident(g3,g0)
    c: Vertical(g0)
    c: Vertical(g2)
    c: Horizontal(g1)
    c: Horizontal(g3)
    c: DistanceX(g3,g3) = 3
    c: DistanceY(g2,g2) = 1.5
    c: Coincident(g4,g5)
    c: Coincident(g5,g6)
    c: Coincident(g6,g7)
    c: Coincident(g7,g4)
    c: Vertical(g4)
    c: Vertical(g6)
    c: Horizontal(g5)
    c: Horizontal(g7)
    c: Equal(g5,g3)
    c: Equal(g6,g2)
    c: PointOnObject(g2,g6)
    c: DistanceY(g2,g5) = 19.8
    c: DistanceY(g-1,g2) = 18
    c: DistanceX(g-1,g0) = 81.8
FEATURE [PartDesign::LinearPattern] LinearPattern
  Direction = -> Sketch032 [H_Axis]
  Length = 57
  Length2 = 100
  Mode = 1
  Mode2 = 0
  Occurrences = 4
  Occurrences2 = 1
  Offset = 19
  Offset2 = 10
  Refine = true
  Reversed = true
  Reversed2 = false
  SpacingPattern = [0]
  SpacingPattern2 = [0]
  Spacings = [-1,-1,-1]
  Suppressed = false
  TransformMode = 0
  expr: Occurrences = <<Params>>.keystoneBackX
  expr: Offset = <<Params>>.keystoneHoleWidth + 4.2
FEATURE [App::Link] Front_cover  label="Front cover001"
  LinkPlacement = pos=(-1.29e-14,-90,2e-16) rot=(0,0,1;0rad)
  LinkedObject = -> Part006
  Placement = pos=(-1.29e-14,-90,2e-16) rot=(0,0,1;0rad)
FEATURE [App::Link] Top_Cover  label="Top Cover001"
  LinkPlacement = pos=(-0.125,-0.875,42) rot=(0,0,1;0rad)
  LinkedObject = -> Part007
  Placement = pos=(-0.125,-0.875,42) rot=(0,0,1;0rad)
FEATURE [App::FeaturePython] Joint  label="Fixed"  # Assembly joint (typed FeaturePython)
  Angle = 0
  AngleMax = 0
  AngleMin = 0
  Detach1 = false
  Detach2 = false
  Distance = 0
  Distance2 = 0
  EnableAngleMax = false
  EnableAngleMin = false
  EnableLengthMax = false
  EnableLengthMin = false
  JointType = 0 (Fixed)
  LengthMax = 0
  LengthMin = 0
  Placement1 = pos=(-96.15,-90,9.5) rot=(1,0,0;1.5708rad)
  Placement2 = pos=(-96.15,-2.1e-15,9.5) rot=(1,0,0;1.5708rad)
  Reference1 = -> Assembly [Box.Body.Edge119,Box.Body.Edge119]
  Reference2 = -> Assembly [Front_cover.Body005.Edge2184,Front_cover.Body005.Edge2184]
  Suppressed = false
FEATURE [App::FeaturePython] Joint001  label="Fixed001"  # Assembly joint (typed FeaturePython)
  Angle = 0
  AngleMax = 0
  AngleMin = 0
  Detach1 = false
  Detach2 = false
  Distance = 0
  Distance2 = 0
  EnableAngleMax = false
  EnableAngleMin = false
  EnableLengthMax = false
  EnableLengthMin = false
  JointType = 0 (Fixed)
  LengthMax = 0
  LengthMin = 0
  Placement1 = pos=(-96.15,-72.4,42) rot=(1,0,0;3.14159rad)
  Placement2 = pos=(-96.025,-71.525,0) rot=(0,0,1;0rad)
  Reference1 = -> Assembly [Box.Body.Edge44,Box.Body.Edge44]
  Reference2 = -> Assembly [Top_Cover.Body006.Edge14,Top_Cover.Body006.Edge14]
  Suppressed = false
FEATURE [App::Link] Ear_3D  label="Ear 3D001"
  LinkPlacement = pos=(-105,-92,0) rot=(0,0,1;3.14159rad)
  LinkedObject = -> Part005
  Placement = pos=(-105,-92,0) rot=(0,0,1;3.14159rad)
FEATURE [App::Link] Ear_3D001  label="Ear 3D002"
  LinkPlacement = pos=(105,-92,44) rot=(1,0,0;3.14159rad)
  LinkedObject = -> Part005
  Placement = pos=(105,-92,44) rot=(1,0,0;3.14159rad)
FEATURE [App::Link] NF_A4x10_FLX001  label="NF-A4x10 FLX001"
  LinkPlacement = pos=(68.8,86.1,22) rot=(0,0.707107,-0.707107;3.14159rad)
  LinkedObject = -> NF_A4x10_FLX
  Placement = pos=(68.8,86.1,22) rot=(0,0.707107,-0.707107;3.14159rad)
FEATURE [App::FeaturePython] Joint004  label="Fixed004"  # Assembly joint (typed FeaturePython)
  Angle = 0
  AngleMax = 0
  AngleMin = 0
  Detach1 = false
  Detach2 = false
  Distance = 0
  Distance2 = 0
  EnableAngleMax = false
  EnableAngleMin = false
  EnableLengthMax = false
  EnableLengthMin = false
  JointType = 0 (Fixed)
  LengthMax = 0
  LengthMin = 0
  Placement1 = pos=(84.8,86.5,6) rot=(1,0,0;1.5708rad)
  Placement2 = pos=(0,0,0) rot=(0,1,0;3.14159rad)
  Reference1 = -> Assembly [Box.Body.Edge162,Box.Body.Edge162]
  Reference2 = -> Assembly [NF_A4x10_FLX001.Part__Feature005.Edge2,NF_A4x10_FLX001.Part__Feature005.Edge2]
  Suppressed = false
FEATURE [App::FeaturePython] Joint006  label="Fixed006"  # Assembly joint (typed FeaturePython)
  Angle = 0
  AngleMax = 0
  AngleMin = 0
  Detach1 = false
  Detach2 = false
  Distance = 0
  Distance2 = 0
  EnableAngleMax = false
  EnableAngleMin = false
  EnableLengthMax = false
  EnableLengthMin = false
  JointType = 0 (Fixed)
  LengthMax = 0
  LengthMin = 0
  Offset1 = pos=(0,-2,0) rot=(0,0,1;0rad)
  Offset2 = pos=(0,0,0) rot=(0,0,1;3.14159rad)
  Placement1 = pos=(-105,-92,0) rot=(0,0,1;0rad)
  Placement2 = pos=(0,0,0) rot=(0,0,1;3.14159rad)
  Reference1 = -> Assembly [Box.Body.Edge110,Box.Body.Vertex93]
  Reference2 = -> Assembly [Ear_3D.Body004.Edge25,Ear_3D.Body004.Vertex5]
  Suppressed = false
  expr: .Offset1.Base.y = -<<Params>>.frontThickness
FEATURE [App::FeaturePython] Joint007  label="Fixed007"  # Assembly joint (typed FeaturePython)
  Angle = 0
  AngleMax = 0
  AngleMin = 0
  Detach1 = false
  Detach2 = false
  Distance = 0
  Distance2 = 0
  EnableAngleMax = false
  EnableAngleMin = false
  EnableLengthMax = false
  EnableLengthMin = false
  JointType = 0 (Fixed)
  LengthMax = 0
  LengthMin = 0
  Offset1 = pos=(0,-2,0) rot=(0,0,1;0rad)
  Placement1 = pos=(105,-92,0) rot=(0,0,1;0rad)
  Placement2 = pos=(-4.4e-14,1.47e-14,44) rot=(0,0,1;0rad)
  Reference1 = -> Assembly [Box.Body.Edge111,Box.Body.Vertex94]
  Reference2 = -> Assembly [Ear_3D001.Body004.Edge25,Ear_3D001.Body004.Vertex22]
  Suppressed = false
  expr: .Offset1.Base.y = -<<Params>>.frontThickness
FEATURE [Part::Feature] Part__Feature033  label="powerpole 15-45A housing"
  shape: bbox 9.2 x 9.2 x 24.75 mm, 117 faces (baked)
FEATURE [App::Part] Part002  label="RED AP"
  Group = -> [Part__Feature033]
  Origin = -> Origin004
  Placement = pos=(-26.1,0.125,-3.75) rot=(0,0,1;0rad)
FEATURE [Part::Feature] Part__Feature034  label="powerpole 15-45A housing001"
  shape: bbox 9.2 x 9.2 x 24.75 mm, 117 faces (baked)
FEATURE [App::Part] Part003  label="BLACK AP"
  Group = -> [Part__Feature034]
  Origin = -> Origin005
  Placement = pos=(-17.6,0.125,-3.75) rot=(0,0,1;0rad)
FEATURE [Part::FeaturePython] Screw  label="M3x8-Screw"  # WARN: FeaturePython — macro-defined, semantics opaque (R4)
  Diameter = 3
  Invert = false
  LeftHanded = false
  Length = 0
  LengthCustom = 8
  MatchOuter = false
  OffsetAngle = 0
  Placement = pos=(-96.15,-92.0514,34.5) rot=(1,0,0;1.5708rad)
  Thread = false
  Type = 51
FEATURE [App::FeaturePython] Joint011  label="Fixed011"  # Assembly joint (typed FeaturePython)
  Angle = 0
  AngleMax = 0
  AngleMin = 0
  Detach1 = false
  Detach2 = false
  Distance = 0
  Distance2 = 0
  EnableAngleMax = false
  EnableAngleMin = false
  EnableLengthMax = false
  EnableLengthMin = false
  JointType = 0 (Fixed)
  LengthMax = 0
  LengthMin = 0
  Placement1 = pos=(0,0,-1.90142) rot=(0,0,1;0rad)
  Placement2 = pos=(-96.15,-0.15,34.5) rot=(1,0,0;1.5708rad)
  Reference1 = -> Assembly [Screw.Edge4,Screw.Edge4]
  Reference2 = -> Assembly [Front_cover.Body005.Edge2101,Front_cover.Body005.Edge2101]
  Suppressed = false
FEATURE [Part::FeaturePython] Screw001  label="M3x6-Screw"  # WARN: FeaturePython — macro-defined, semantics opaque (R4)
  Diameter = 3
  Invert = false
  LeftHanded = false
  Length = 7
  LengthCustom = 6
  MatchOuter = false
  OffsetAngle = 0
  Placement = pos=(-107.981,-42.4,34.5) rot=(0.57735,-0.57735,-0.57735;2.0944rad)
  Thread = false
  Type = 51
FEATURE [App::FeaturePython] Joint012  label="Fixed012"  # Assembly joint (typed FeaturePython)
  Angle = 0
  AngleMax = 0
  AngleMin = 0
  Detach1 = false
  Detach2 = false
  Distance = 0
  Distance2 = 0
  EnableAngleMax = false
  EnableAngleMin = false
  EnableLengthMax = false
  EnableLengthMin = false
  JointType = 0 (Fixed)
  LengthMax = 0
  LengthMin = 0
  Placement1 = pos=(0,0,-1.83071) rot=(0,0,1;0rad)
  Placement2 = pos=(1.15,-49.6,34.5) rot=(0.57735,0.57735,0.57735;2.0944rad)
  Reference1 = -> Assembly [Screw001.Edge6,Screw001.Edge6]
  Reference2 = -> Assembly [Ear_3D.Body004.Edge67,Ear_3D.Body004.Edge67]
  Suppressed = false
FEATURE [Part::FeaturePython] Screw002  label="M3x6-Screw021"  # WARN: FeaturePython — macro-defined, semantics opaque (R4)
  Diameter = 3
  Invert = false
  LeftHanded = false
  Length = 7
  LengthCustom = 6
  MatchOuter = false
  OffsetAngle = 0
  Placement = pos=(-107.981,-72.4,34.5) rot=(0.57735,-0.57735,-0.57735;2.0944rad)
  Thread = false
  Type = 51
FEATURE [App::FeaturePython] Joint013  label="Fixed013"  # Assembly joint (typed FeaturePython)
  Angle = 0
  AngleMax = 0
  AngleMin = 0
  Detach1 = false
  Detach2 = false
  Distance = 0
  Distance2 = 0
  EnableAngleMax = false
  EnableAngleMin = false
  EnableLengthMax = false
  EnableLengthMin = false
  JointType = 0 (Fixed)
  LengthMax = 0
  LengthMin = 0
  Placement1 = pos=(0,0,-1.83071) rot=(0,0,1;0rad)
  Placement2 = pos=(1.15,-19.6,34.5) rot=(0.57735,0.57735,0.57735;2.0944rad)
  Reference1 = -> Assembly [Screw002.Edge6,Screw002.Edge6]
  Reference2 = -> Assembly [Ear_3D.Body004.Edge63,Ear_3D.Body004.Edge63]
  Suppressed = false
FEATURE [Part::FeaturePython] Screw003  label="M3x6-Screw006"  # WARN: FeaturePython — macro-defined, semantics opaque (R4)
  Diameter = 3
  Invert = false
  LeftHanded = false
  Length = 7
  LengthCustom = 6
  MatchOuter = false
  OffsetAngle = 0
  Placement = pos=(-104.319,-42.4,9.5) rot=(0.57735,0.57735,0.57735;2.0944rad)
  Thread = false
  Type = 51
FEATURE [Part::FeaturePython] Screw004  label="M3x8-Screw003"  # WARN: FeaturePython — macro-defined, semantics opaque (R4)
  Diameter = 3
  Invert = false
  LeftHanded = false
  Length = 0
  LengthCustom = 8
  MatchOuter = false
  OffsetAngle = 0
  Placement = pos=(96.15,-91.9807,34.5) rot=(1,0,0;1.5708rad)
  Thread = false
  Type = 51
FEATURE [App::FeaturePython] Joint015  label="Fixed015"  # Assembly joint (typed FeaturePython)
  Angle = 0
  AngleMax = 0
  AngleMin = 0
  Detach1 = false
  Detach2 = false
  Distance = 0
  Distance2 = 0
  EnableAngleMax = false
  EnableAngleMin = false
  EnableLengthMax = false
  EnableLengthMin = false
  JointType = 0 (Fixed)
  LengthMax = 0
  LengthMin = 0
  Placement1 = pos=(0,0,-1.83071) rot=(0,0,1;0rad)
  Placement2 = pos=(96.15,-0.15,34.5) rot=(1,0,0;1.5708rad)
  Reference1 = -> Assembly [Screw004.Edge6,Screw004.Edge6]
  Reference2 = -> Assembly [Front_cover.Body005.Edge1146,Front_cover.Body005.Edge1146]
  Suppressed = false
FEATURE [Part::FeaturePython] Screw005  label="M3x8-Screw004"  # WARN: FeaturePython — macro-defined, semantics opaque (R4)
  Diameter = 3
  Invert = false
  LeftHanded = false
  Length = 0
  LengthCustom = 8
  MatchOuter = false
  OffsetAngle = 0
  Placement = pos=(-96.15,-91.9807,9.5) rot=(1,0,0;1.5708rad)
  Thread = false
  Type = 51
FEATURE [App::FeaturePython] Joint016  label="Fixed016"  # Assembly joint (typed FeaturePython)
  Angle = 0
  AngleMax = 0
  AngleMin = 0
  Detach1 = false
  Detach2 = false
  Distance = 0
  Distance2 = 0
  EnableAngleMax = false
  EnableAngleMin = false
  EnableLengthMax = false
  EnableLengthMin = false
  JointType = 0 (Fixed)
  LengthMax = 0
  LengthMin = 0
  Placement1 = pos=(0,0,-1.83071) rot=(0,0,1;0rad)
  Placement2 = pos=(-96.15,-0.15,9.5) rot=(1,0,0;1.5708rad)
  Reference1 = -> Assembly [Screw005.Edge6,Screw005.Edge6]
  Reference2 = -> Assembly [Front_cover.Body005.Edge1666,Front_cover.Body005.Edge1666]
  Suppressed = false
FEATURE [Part::FeaturePython] Screw006  label="M3x8-Screw005"  # WARN: FeaturePython — macro-defined, semantics opaque (R4)
  Diameter = 3
  Invert = false
  LeftHanded = false
  Length = 0
  LengthCustom = 8
  MatchOuter = false
  OffsetAngle = 0
  Placement = pos=(96.15,-91.9807,9.5) rot=(1,0,0;1.5708rad)
  Thread = false
  Type = 51
FEATURE [App::FeaturePython] Joint017  label="Fixed017"  # Assembly joint (typed FeaturePython)
  Angle = 0
  AngleMax = 0
  AngleMin = 0
  Detach1 = false
  Detach2 = false
  Distance = 0
  Distance2 = 0
  EnableAngleMax = false
  EnableAngleMin = false
  EnableLengthMax = false
  EnableLengthMin = false
  JointType = 0 (Fixed)
  LengthMax = 0
  LengthMin = 0
  Placement1 = pos=(0,0,-1.83071) rot=(0,0,1;0rad)
  Placement2 = pos=(96.15,-0.15,9.5) rot=(1,0,0;1.5708rad)
  Reference1 = -> Assembly [Screw006.Edge6,Screw006.Edge6]
  Reference2 = -> Assembly [Front_cover.Body005.Edge729,Front_cover.Body005.Edge729]
  Suppressed = false
FEATURE [App::FeaturePython] Joint018  label="Fixed018"  # Assembly joint (typed FeaturePython)
  Angle = 0
  AngleMax = 0
  AngleMin = 0
  Detach1 = false
  Detach2 = false
  Distance = 0
  Distance2 = 0
  EnableAngleMax = false
  EnableAngleMin = false
  EnableLengthMax = false
  EnableLengthMin = false
  JointType = 0 (Fixed)
  LengthMax = 0
  LengthMin = 0
  Placement1 = pos=(0,-1.42e-14,-1.83071) rot=(0,0,1;0rad)
  Placement2 = pos=(1.15,-49.6,9.5) rot=(0.57735,0.57735,0.57735;2.0944rad)
  Reference1 = -> Assembly [Screw003.Edge6,Screw003.Edge6]
  Reference2 = -> Assembly [Ear_3D.Body004.Edge65,Ear_3D.Body004.Edge65]
  Suppressed = false
FEATURE [Part::FeaturePython] Screw007  label="M3x6-Screw022"  # WARN: FeaturePython — macro-defined, semantics opaque (R4)
  Diameter = 3
  Invert = false
  LeftHanded = false
  Length = 7
  LengthCustom = 6
  MatchOuter = false
  OffsetAngle = 0
  Placement = pos=(-107.981,-72.4,9.5) rot=(0.57735,-0.57735,-0.57735;2.0944rad)
  Thread = false
  Type = 51
FEATURE [App::FeaturePython] Joint019  label="Fixed019"  # Assembly joint (typed FeaturePython)
  Angle = 0
  AngleMax = 0
  AngleMin = 0
  Detach1 = false
  Detach2 = false
  Distance = 0
  Distance2 = 0
  EnableAngleMax = false
  EnableAngleMin = false
  EnableLengthMax = false
  EnableLengthMin = false
  JointType = 0 (Fixed)
  LengthMax = 0
  LengthMin = 0
  Placement1 = pos=(0,0,-1.83071) rot=(0,0,1;0rad)
  Placement2 = pos=(1.15,-19.6,9.5) rot=(0.57735,0.57735,0.57735;2.0944rad)
  Reference1 = -> Assembly [Screw007.Edge6,Screw007.Edge6]
  Reference2 = -> Assembly [Ear_3D.Body004.Edge61,Ear_3D.Body004.Edge61]
  Suppressed = false
FEATURE [Sketcher::SketchObject] Sketch037
  ArcFitTolerance = 1e-06
  AttachmentSupport = -> [Chamfer004]
  ExternalTypes = [0]
  FullyConstrained = true
  MakeInternals = false
  MapMode = 5
  Placement = pos=(0,-2,0) rot=(1,0,0;1.5708rad)
  expr: Constraints[11] = <<Params>>.boxWidth - 2 * (<<Params>>.fitTol + <<Params>>.wallThickness + 5 + <<Params>>.M3InsertDiam + 5)
  expr: Constraints[13] = (<<Params>>.rackUnit * <<Params>>.boxHeight - <<Params>>.rackUnitTolerance) / 2
  expr: Constraints[8] = <<Params>>.rackUnit * <<Params>>.boxHeight - <<Params>>.rackUnitTolerance - 2 * <<Params>>.wallThickness - 2 * <<Params>>.fitTol
  sketch-geometry (6):
    g0: LineSegment StartX=-88.8 StartY=42 StartZ=0 EndX=-88.8 EndY=2 EndZ=0
    g1: LineSegment StartX=-88.8 StartY=2 StartZ=0 EndX=88.8 EndY=2 EndZ=0
    g2: LineSegment StartX=88.8 StartY=2 StartZ=0 EndX=88.8 EndY=42 EndZ=0
    g3: LineSegment StartX=88.8 StartY=42 StartZ=0 EndX=-88.8 EndY=42 EndZ=0
    g4: GeomPoint X=0 Y=2 Z=0
    g5: GeomPoint X=88.8 Y=22 Z=0
  constraints (14):
    c: Coincident(g0,g1)
    c: Coincident(g1,g2)
    c: Coincident(g2,g3)
    c: Coincident(g3,g0)
    c: Vertical(g0)
    c: Vertical(g2)
    c: Horizontal(g1)
    c: Horizontal(g3)
    c: DistanceY(g2,g2) = 40
    c: Symmetric(g1,g1,g4)
    c: PointOnObject(g4,g-2)
    c: DistanceX(g3,g3) = 177.6
    c: Symmetric(g2,g2,g5)
    c: DistanceY(g-1,g5) = 22
FEATURE [PartDesign::Pad] Pad015
  BaseFeature = -> Chamfer004
  Direction = (0,-1,2e-16)
  Length = 3.75
  Length2 = 10
  Placement = pos=(0,0,0) rot=(1,0,0;1.5708rad)
  Profile = -> Sketch037
  ReferenceAxis = -> Sketch037 [N_Axis]
  Refine = true
  Reversed = true
  SideType = 0
  Suppressed = false
  Type = 0
  Type2 = 0
  expr: Length = <<Params>>.frontThickness + <<Params>>.wallThickness
FEATURE [PartDesign::Pocket] Pocket007  label="VentHolePocket"
  BaseFeature = -> Pad015
  Direction = (0,-1,-2e-16)
  Length = 2
  Length2 = 1.75
  Placement = pos=(0,0,0) rot=(1,0,0;1.5708rad)
  Profile = -> Sketch017
  ReferenceAxis = -> Sketch017 [N_Axis]
  Refine = true
  SideType = 1
  Suppressed = false
  Type = 0
  Type2 = 0
  expr: Length = <<Params>>.frontThickness
  expr: Length2 = <<Params>>.wallThickness
FEATURE [PartDesign::MultiTransform] MultiTransform002  label="VentHolesTransform"
  BaseFeature = -> Pocket007
  Originals = -> [Pocket007]
  Placement = pos=(0,0,0) rot=(1,0,0;1.5708rad)
  Refine = true
  Suppressed = false
  TransformMode = 0
  Transformations = -> [LinearPattern005,LinearPattern006,Mirrored003,Mirrored004]
FEATURE [Sketcher::SketchObject] Sketch018  label="MinContour"
  ArcFitTolerance = 1e-06
  AttachmentSupport = -> [Pad015]
  ExternalTypes = [0]
  FullyConstrained = true
  MakeInternals = false
  MapMode = 5
  Placement = pos=(0,-2,9e-16) rot=(1,0,0;1.5708rad)
  expr: Constraints[22] = <<Params>>.boxHeight * <<Params>>.rackUnit - <<Params>>.rackUnitTolerance - 2 * <<Params>>.wallThickness
  expr: Constraints[25] = <<Params>>.boxWidth - 2 * (5 + 5 + <<Params>>.M3InsertDiam + <<Params>>.wallThickness)
  expr: Constraints[8] = <<Params>>.wallThickness
  sketch-geometry (11):
    g0: LineSegment StartX=-89.05 StartY=42.25 StartZ=0 EndX=89.05 EndY=42.25 EndZ=0
    g1: LineSegment StartX=89.05 StartY=42.25 StartZ=0 EndX=89.05 EndY=44 EndZ=0
    g2: LineSegment StartX=89.05 StartY=44 StartZ=0 EndX=-89.05 EndY=44 EndZ=0
    g3: LineSegment StartX=-89.05 StartY=44 StartZ=0 EndX=-89.05 EndY=42.25 EndZ=0
    g4: LineSegment [constr] StartX=-89.05 StartY=42.25 StartZ=0 EndX=-89.05 EndY=0 EndZ=0
    g5: LineSegment [constr] StartX=89.05 StartY=42.25 StartZ=0 EndX=89.05 EndY=1.75 EndZ=0
    g6: LineSegment StartX=-89.05 StartY=0 StartZ=0 EndX=89.05 EndY=0 EndZ=0
    g7: LineSegment StartX=89.05 StartY=0 StartZ=0 EndX=89.05 EndY=1.75 EndZ=0
    g8: LineSegment StartX=89.05 StartY=1.75 StartZ=0 EndX=-89.05 EndY=1.75 EndZ=0
    g9: LineSegment StartX=-89.05 StartY=1.75 StartZ=0 EndX=-89.05 EndY=0 EndZ=0
    g10: GeomPoint X=0 Y=0 Z=0
  constraints (29):
    c: Coincident(g0,g1)
    c: Coincident(g1,g2)
    c: Coincident(g2,g3)
    c: Coincident(g3,g0)
    c: Horizontal(g0)
    c: Horizontal(g2)
    c: Vertical(g1)
    c: Vertical(g3)
    c: DistanceY(g1,g1) = 1.75
    c: Coincident(g4,g0)
    c: Vertical(g4)
    c: Coincident(g5,g0)
    c: Vertical(g5)
    c: Coincident(g6,g7)
    c: Coincident(g7,g8)
    c: Coincident(g8,g9)
    c: Coincident(g9,g6)
    c: Horizontal(g6)
    c: Horizontal(g8)
    c: Vertical(g7)
    c: Vertical(g9)
    c: Coincident(g6,g4)
    c: DistanceY(g7,g0) = 40.5
    c: Equal(g9,g3)
    c: PointOnObject(g-1,g6)
    c: DistanceX(g2,g2) = 178.1
    c: Coincident(g5,g7)
    c: Symmetric(g6,g6,g10)
    c: PointOnObject(g10,g-2)
FEATURE [PartDesign::Pad] Pad010  label="MinContourPad"
  BaseFeature = -> MultiTransform002
  Direction = (0,-1,2e-16)
  Length = 10
  Length2 = 10
  Placement = pos=(0,0,0) rot=(1,0,0;1.5708rad)
  Profile = -> Sketch018
  ReferenceAxis = -> Sketch018 [N_Axis]
  Refine = true
  SideType = 0
  Suppressed = false
  Type = 3
  Type2 = 0
  UpToFace = -> Pad015 [Face3]
FEATURE [PartDesign::Pad] Pad011  label="KeystoneHolderSlabPad"
  BaseFeature = -> Pad010
  Direction = (0,-1,2e-16)
  Length = 9.75
  Length2 = 10
  Placement = pos=(0,0,0) rot=(1,0,0;1.5708rad)
  Profile = -> Sketch019
  ReferenceAxis = -> Sketch019 [N_Axis]
  Refine = true
  Reversed = true
  SideType = 0
  Suppressed = false
  Type = 0
  Type2 = 0
  expr: Length = <<Params>>.keystoneStopDepth
FEATURE [Sketcher::SketchObject] Sketch020  label="KeystoneHole"
  ArcFitTolerance = 1e-06
  AttachmentSupport = -> [Pad011]
  ExternalTypes = [0]
  FullyConstrained = true
  MakeInternals = false
  MapMode = 5
  Placement = pos=(0,7.75,-1.7e-15) rot=(-1,0,0;1.5708rad)
  expr: Constraints[10] = <<Params>>.wallThickness + 2 + 3
  expr: Constraints[11] = min(4.2 + (4.2 + <<Params>>.keystoneHoleWidth) * <<Params>>.keystoneFrontX; <<Params>>.boxWidth - 2 * (<<Params>>.wallThickness * 2 + 10 + <<Params>>.M3InsertDiam)) / 2 - 4.2
  expr: Constraints[8] = <<Params>>.keystoneHoleWidth
  expr: Constraints[9] = <<Params>>.keystoneHoleHeight
  sketch-geometry (4):
    g0: LineSegment StartX=-45.4 StartY=-6.75 StartZ=0 EndX=-45.4 EndY=-23.55 EndZ=0
    g1: LineSegment StartX=-45.4 StartY=-23.55 StartZ=0 EndX=-30.6 EndY=-23.55 EndZ=0
    g2: LineSegment StartX=-30.6 StartY=-23.55 StartZ=0 EndX=-30.6 EndY=-6.75 EndZ=0
    g3: LineSegment StartX=-30.6 StartY=-6.75 StartZ=0 EndX=-45.4 EndY=-6.75 EndZ=0
  constraints (12):
    c: Coincident(g0,g1)
    c: Coincident(g1,g2)
    c: Coincident(g2,g3)
    c: Coincident(g3,g0)
    c: Vertical(g0)
    c: Vertical(g2)
    c: Horizontal(g1)
    c: Horizontal(g3)
    c: DistanceX(g3,g3) = 14.8
    c: DistanceY(g2,g2) = 16.8
    c: DistanceY(g0,g-1) = 6.75
    c: DistanceX(g0,g-1) = 45.4
FEATURE [PartDesign::Pocket] Pocket008  label="KeystoneHolePocket"
  BaseFeature = -> Pad011
  Direction = (0,-1,-2e-16)
  Length = 5
  Length2 = 5
  Placement = pos=(0,0,0) rot=(1,0,0;1.5708rad)
  Profile = -> Sketch020
  ReferenceAxis = -> Sketch020 [N_Axis]
  Refine = true
  SideType = 0
  Suppressed = false
  Type = 1
  Type2 = 0
FEATURE [Sketcher::SketchObject] Sketch021  label="KeystoneCatchDepth"
  ArcFitTolerance = 1e-06
  AttachmentSupport = -> [Pocket008]
  ExternalTypes = [0]
  FullyConstrained = true
  MakeInternals = false
  MapMode = 5
  Placement = pos=(0,7.75,-1.7e-15) rot=(-1,0,0;1.5708rad)
  expr: Constraints[10] = <<Params>>.wallThickness * 2 + <<Params>>.fitTol + 3
  expr: Constraints[11] = min(4.2 + (4.2 + <<Params>>.keystoneHoleWidth) * <<Params>>.keystoneFrontX; <<Params>>.boxWidth - 2 * (<<Params>>.wallThickness * 2 + 10 + <<Params>>.M3InsertDiam)) / 2 - 4.2
  expr: Constraints[8] = <<Params>>.keystoneHoleWidth
  expr: Constraints[9] = <<Params>>.keystoneCatchHeight
  sketch-geometry (4):
    g0: LineSegment StartX=-45.4 StartY=-26.55 StartZ=0 EndX=-30.6 EndY=-26.55 EndZ=0
    g1: LineSegment StartX=-30.6 StartY=-26.55 StartZ=0 EndX=-30.6 EndY=-6.75 EndZ=0
    g2: LineSegment StartX=-30.6 StartY=-6.75 StartZ=0 EndX=-45.4 EndY=-6.75 EndZ=0
    g3: LineSegment StartX=-45.4 StartY=-6.75 StartZ=0 EndX=-45.4 EndY=-26.55 EndZ=0
  constraints (12):
    c: Coincident(g0,g1)
    c: Coincident(g1,g2)
    c: Coincident(g2,g3)
    c: Coincident(g3,g0)
    c: Horizontal(g0)
    c: Horizontal(g2)
    c: Vertical(g1)
    c: Vertical(g3)
    c: Distance(g2,g2) = 14.8
    c: DistanceY(g1,g1) = 19.8
    c: DistanceY(g1,g-1) = 6.75
    c: DistanceX(g2,g-1) = 45.4
FEATURE [PartDesign::Pocket] Pocket009  label="KeystoneCatchDepthPocket"
  BaseFeature = -> Pocket008
  Direction = (0,-1,-2e-16)
  Length = 8.2
  Length2 = 5
  Placement = pos=(0,0,0) rot=(1,0,0;1.5708rad)
  Profile = -> Sketch021
  ReferenceAxis = -> Sketch021 [N_Axis]
  Refine = true
  SideType = 0
  Suppressed = false
  Type = 0
  Type2 = 0
  expr: Length = <<Params>>.keystoneCatchDepth
FEATURE [Sketcher::SketchObject] Sketch022  label="CatchHoles"
  ArcFitTolerance = 1e-06
  AttachmentSupport = -> [Pocket009]
  ExternalTypes = [0]
  FullyConstrained = true
  MakeInternals = false
  MapMode = 5
  Placement = pos=(-49.6,0,0) rot=(0.707107,0,-0.707107;3.14159rad)
  expr: Constraints[19] = <<Params>>.keystoneCatchHeight
  expr: Constraints[23] = <<Params>>.keystoneCatchDepth - <<Params>>.frontThickness
  sketch-geometry (8):
    g0: LineSegment StartX=-28.05 StartY=-6.2 StartZ=0 EndX=-26.55 EndY=-6.2 EndZ=0
    g1: LineSegment StartX=-26.55 StartY=-6.2 StartZ=0 EndX=-26.55 EndY=-3.2 EndZ=0
    g2: LineSegment StartX=-26.55 StartY=-3.2 StartZ=0 EndX=-28.05 EndY=-3.2 EndZ=0
    g3: LineSegment StartX=-28.05 StartY=-3.2 StartZ=0 EndX=-28.05 EndY=-6.2 EndZ=0
    g4: LineSegment StartX=-6.75 StartY=-3.2 StartZ=0 EndX=-6.75 EndY=-6.2 EndZ=0
    g5: LineSegment StartX=-6.75 StartY=-6.2 StartZ=0 EndX=-5.25 EndY=-6.2 EndZ=0
    g6: LineSegment StartX=-5.25 StartY=-6.2 StartZ=0 EndX=-5.25 EndY=-3.2 EndZ=0
    g7: LineSegment StartX=-5.25 StartY=-3.2 StartZ=0 EndX=-6.75 EndY=-3.2 EndZ=0
  constraints (24):
    c: Coincident(g0,g1)
    c: Coincident(g1,g2)
    c: Coincident(g2,g3)
    c: Coincident(g3,g0)
    c: Horizontal(g0)
    c: Horizontal(g2)
    c: Vertical(g1)
    c: Vertical(g3)
    c: Coincident(g4,g5)
    c: Coincident(g5,g6)
    c: Coincident(g6,g7)
    c: Coincident(g7,g4)
    c: Vertical(g4)
    c: Vertical(g6)
    c: Horizontal(g5)
    c: Horizontal(g7)
    c: Equal(g7,g0)
    c: Equal(g4,g3)
    c: DistanceX(g5,g5) = 1.5
    c: DistanceX(g1,g4) = 19.8
    c: DistanceX(g4,g-1) = 6.75
    c: PointOnObject(g4,g2)
    c: DistanceY(g4,g4) = 3
    c: DistanceY(g5,g-1) = 6.2
FEATURE [PartDesign::Pocket] Pocket010  label="CatchHolesPocket"
  BaseFeature = -> Pocket009
  Direction = (1,0,2e-16)
  Length = 19
  Length2 = -4.2
  Placement = pos=(0,0,0) rot=(1,0,0;1.5708rad)
  Profile = -> Sketch022
  ReferenceAxis = -> Sketch022 [N_Axis]
  Refine = true
  SideType = 1
  Suppressed = false
  Type = 0
  Type2 = 0
  expr: Length = <<Params>>.keystoneHoleWidth + 4.2
  expr: Length2 = -4.2
FEATURE [PartDesign::Chamfer] Chamfer005  label="KeystoneInsertChamfer"
  Angle = 45
  Base = -> Pocket010 [Edge2134,Edge1712,Edge2132]
  BaseFeature = -> Pocket010
  ChamferType = 0
  FlipDirection = false
  Placement = pos=(0,0,0) rot=(1,0,0;1.5708rad)
  Refine = true
  Size = 1
  Size2 = 1
  SupportTransform = false
  Suppressed = false
  UseAllEdges = false
FEATURE [PartDesign::MultiTransform] MultiTransform006
  BaseFeature = -> Chamfer005
  Originals = -> [Pocket010,Chamfer005,Pocket009,Pocket008]
  Placement = pos=(0,0,0) rot=(1,0,0;1.5708rad)
  Refine = true
  Suppressed = false
  TransformMode = 0
  Transformations = -> [LinearPattern013,LinearPattern014]
FEATURE [PartDesign::Body] Body005  label="frontCoverVented001"
  AllowCompound = false
  Group = -> [Sketch016,Pad009,Chamfer004,Sketch017,Sketch037,Pad015,Pocket007,LinearPattern005,LinearPattern006,Sketch018,Mirrored003,DatumPlane001,Mirrored004,MultiTransform002,Pad010,Sketch019,Pad011,Sketch020,Pocket008,Sketch021,Pocket009,Sketch022,Pocket010,Chamfer005,MultiTransform006,LinearPattern013,LinearPattern014]
  Origin = -> Origin019
  Tip = -> MultiTransform006
FEATURE [App::Part] Part006  label="Front cover"
  Group = -> [Body005]
  Origin = -> Origin018
  Placement = pos=(0,-1.42e-14,0) rot=(0,0,1;0rad)
FEATURE [Part::FeaturePython] Screw008  label="M3x6-Screw023"  # WARN: FeaturePython — macro-defined, semantics opaque (R4)
  Diameter = 3
  Invert = false
  LeftHanded = false
  Length = 7
  LengthCustom = 6
  MatchOuter = false
  OffsetAngle = 0
  Placement = pos=(107.981,-42.4,34.5) rot=(0.57735,-0.57735,0.57735;4.18879rad)
  Thread = false
  Type = 51
FEATURE [App::FeaturePython] Joint021  label="Fixed021"  # Assembly joint (typed FeaturePython)
  Angle = 0
  AngleMax = 0
  AngleMin = 0
  Detach1 = false
  Detach2 = false
  Distance = 0
  Distance2 = 0
  EnableAngleMax = false
  EnableAngleMin = false
  EnableLengthMax = false
  EnableLengthMin = false
  JointType = 0 (Fixed)
  LengthMax = 0
  LengthMin = 0
  Placement1 = pos=(0,0,-1.83071) rot=(0,0,1;0rad)
  Placement2 = pos=(1.15,-49.6,9.5) rot=(0.57735,0.57735,0.57735;2.0944rad)
  Reference1 = -> Assembly [Screw008.Edge6,Screw008.Edge6]
  Reference2 = -> Assembly [Ear_3D001.Body004.Edge65,Ear_3D001.Body004.Edge65]
  Suppressed = false
FEATURE [Part::FeaturePython] Screw009  label="M3x6-Screw024"  # WARN: FeaturePython — macro-defined, semantics opaque (R4)
  Diameter = 3
  Invert = false
  LeftHanded = false
  Length = 7
  LengthCustom = 6
  MatchOuter = false
  OffsetAngle = 0
  Placement = pos=(107.981,-72.4,34.5) rot=(-0.57735,0.57735,-0.57735;2.0944rad)
  Thread = false
  Type = 51
FEATURE [App::FeaturePython] Joint022  label="Fixed022"  # Assembly joint (typed FeaturePython)
  Angle = 0
  AngleMax = 0
  AngleMin = 0
  Detach1 = false
  Detach2 = false
  Distance = 0
  Distance2 = 0
  EnableAngleMax = false
  EnableAngleMin = false
  EnableLengthMax = false
  EnableLengthMin = false
  JointType = 0 (Fixed)
  LengthMax = 0
  LengthMin = 0
  Placement1 = pos=(0,0,-1.83071) rot=(0,0,1;0rad)
  Placement2 = pos=(1.15,-19.6,9.5) rot=(0.57735,0.57735,0.57735;2.0944rad)
  Reference1 = -> Assembly [Screw009.Edge6,Screw009.Edge6]
  Reference2 = -> Assembly [Ear_3D001.Body004.Edge61,Ear_3D001.Body004.Edge61]
  Suppressed = false
FEATURE [Part::FeaturePython] Screw010  label="M3x6-Screw025"  # WARN: FeaturePython — macro-defined, semantics opaque (R4)
  Diameter = 3
  Invert = false
  LeftHanded = false
  Length = 7
  LengthCustom = 6
  MatchOuter = false
  OffsetAngle = 0
  Placement = pos=(107.981,-42.4,9.5) rot=(0.57735,-0.57735,0.57735;4.18879rad)
  Thread = false
  Type = 51
FEATURE [App::FeaturePython] Joint023  label="Fixed023"  # Assembly joint (typed FeaturePython)
  Angle = 0
  AngleMax = 0
  AngleMin = 0
  Detach1 = false
  Detach2 = false
  Distance = 0
  Distance2 = 0
  EnableAngleMax = false
  EnableAngleMin = false
  EnableLengthMax = false
  EnableLengthMin = false
  JointType = 0 (Fixed)
  LengthMax = 0
  LengthMin = 0
  Placement1 = pos=(0,0,-1.83071) rot=(0,0,1;0rad)
  Placement2 = pos=(1.15,-49.6,34.5) rot=(0.57735,0.57735,0.57735;2.0944rad)
  Reference1 = -> Assembly [Screw010.Edge6,Screw010.Edge6]
  Reference2 = -> Assembly [Ear_3D001.Body004.Edge67,Ear_3D001.Body004.Edge67]
  Suppressed = false
FEATURE [Part::FeaturePython] Screw011  label="M3x6-Screw015"  # WARN: FeaturePython — macro-defined, semantics opaque (R4)
  Diameter = 3
  Invert = false
  LeftHanded = false
  Length = 7
  LengthCustom = 6
  MatchOuter = false
  OffsetAngle = 0
  Placement = pos=(107.981,-72.4,9.5) rot=(-0.57735,0.57735,-0.57735;2.0944rad)
  Thread = false
  Type = 51
FEATURE [App::FeaturePython] Joint024  label="Fixed024"  # Assembly joint (typed FeaturePython)
  Angle = 0
  AngleMax = 0
  AngleMin = 0
  Detach1 = false
  Detach2 = false
  Distance = 0
  Distance2 = 0
  EnableAngleMax = false
  EnableAngleMin = false
  EnableLengthMax = false
  EnableLengthMin = false
  JointType = 0 (Fixed)
  LengthMax = 0
  LengthMin = 0
  Placement1 = pos=(0,0,-1.83071) rot=(0,0,1;0rad)
  Placement2 = pos=(1.15,-19.6,34.5) rot=(0.57735,0.57735,0.57735;2.0944rad)
  Reference1 = -> Assembly [Screw011.Edge6,Screw011.Edge6]
  Reference2 = -> Assembly [Ear_3D001.Body004.Edge63,Ear_3D001.Body004.Edge63]
  Suppressed = false
FEATURE [PartDesign::Chamfer] Chamfer007
  Angle = 45
  Base = -> Pocket006 [Edge132,Edge152,Edge154,Edge134]
  BaseFeature = -> Pocket006
  ChamferType = 0
  FlipDirection = false
  Refine = true
  Size = 1.4
  Size2 = 1
  SupportTransform = false
  Suppressed = false
  UseAllEdges = false
FEATURE [PartDesign::MultiTransform] MultiTransform001
  BaseFeature = -> Chamfer007
  Originals = -> [Pocket006,Chamfer007]
  Refine = true
  Suppressed = false
  TransformMode = 0
  Transformations = -> [LinearPattern003,LinearPattern004]
FEATURE [PartDesign::Pad] Pad012  label="KeystoneSlabPad"
  BaseFeature = -> MultiTransform001
  Direction = (0,1,-2e-16)
  Length = 9.75
  Length2 = 10
  Profile = -> Sketch030
  ReferenceAxis = -> Sketch030 [N_Axis]
  Refine = true
  Reversed = true
  SideType = 0
  Suppressed = false
  Type = 0
  Type2 = 0
  expr: Length = <<Params>>.keystoneStopDepth
FEATURE [PartDesign::Pocket] Pocket011  label="KeystoneHolePocket001"
  BaseFeature = -> Pad012
  Direction = (0,-1,2e-16)
  Length = 5
  Length2 = 5
  Profile = -> Sketch032
  ReferenceAxis = -> Sketch032 [N_Axis]
  Refine = true
  SideType = 0
  Suppressed = false
  Type = 1
  Type2 = 0
FEATURE [Sketcher::SketchObject] Sketch033  label="KeystoneCatchSketch"
  ArcFitTolerance = 1e-06
  AttachmentSupport = -> [Pocket011]
  ExternalTypes = [0]
  FullyConstrained = true
  MakeInternals = false
  MapMode = 5
  Placement = pos=(0,80.25,-4.25e-14) rot=(1,0,0;1.5708rad)
  expr: Constraints[10] = <<Params>>.boxWidth / 2 - (<<Params>>.wallThickness + 5 + <<Params>>.M3InsertDiam + 5) - 4.2
  expr: Constraints[11] = <<Params>>.rackUnit - <<Params>>.rackUnitTolerance - <<Params>>.wallThickness - <<Params>>.keystoneCatchHeight - 4.2 - <<Params>>.fitTol
  expr: Constraints[8] = <<Params>>.keystoneCatchHeight
  expr: Constraints[9] = <<Params>>.keystoneHoleWidth
  sketch-geometry (4):
    g0: LineSegment StartX=-84.85 StartY=37.8 StartZ=0 EndX=-84.85 EndY=18 EndZ=0
    g1: LineSegment StartX=-84.85 StartY=18 StartZ=0 EndX=-70.05 EndY=18 EndZ=0
    g2: LineSegment StartX=-70.05 StartY=18 StartZ=0 EndX=-70.05 EndY=37.8 EndZ=0
    g3: LineSegment StartX=-70.05 StartY=37.8 StartZ=0 EndX=-84.85 EndY=37.8 EndZ=0
  constraints (12):
    c: Coincident(g0,g1)
    c: Coincident(g1,g2)
    c: Coincident(g2,g3)
    c: Coincident(g3,g0)
    c: Vertical(g0)
    c: Vertical(g2)
    c: Horizontal(g1)
    c: Horizontal(g3)
    c: DistanceY(g2,g2) = 19.8
    c: DistanceX(g3,g3) = 14.8
    c: DistanceX(g0,g-1) = 84.85
    c: DistanceY(g-1,g0) = 18
FEATURE [PartDesign::Pocket] Pocket012  label="KeystoneCatchPocket"
  BaseFeature = -> Pocket011
  Direction = (0,1,-2e-16)
  Length = 8.2
  Length2 = 5
  Profile = -> Sketch033
  ReferenceAxis = -> Sketch033 [N_Axis]
  Refine = true
  SideType = 0
  Suppressed = false
  Type = 0
  Type2 = 0
  expr: Length = <<Params>>.keystoneCatchDepth
FEATURE [PartDesign::Pocket] Pocket013  label="CatchHolesPocketBox"
  BaseFeature = -> Pocket012
  Direction = (-1,0,0)
  Length = 19
  Length2 = -4.2
  Profile = -> Sketch034
  ReferenceAxis = -> Sketch034 [N_Axis]
  Refine = true
  Reversed = true
  SideType = 1
  Suppressed = false
  Type = 0
  Type2 = 0
  expr: Length = <<Params>>.keystoneHoleWidth + 4.2
FEATURE [PartDesign::Chamfer] Chamfer006
  Angle = 45
  Base = -> Pocket013 [Edge99,Edge260,Edge97]
  BaseFeature = -> Pocket013
  ChamferType = 0
  FlipDirection = false
  Refine = true
  Size = 1
  Size2 = 1
  SupportTransform = false
  Suppressed = false
  UseAllEdges = false
FEATURE [PartDesign::MultiTransform] MultiTransform
  BaseFeature = -> Chamfer006
  Originals = -> [Pocket011,Pocket012,Pocket013,Chamfer006]
  Refine = true
  Suppressed = false
  TransformMode = 0
  Transformations = -> [LinearPattern]
FEATURE [PartDesign::Body] Body  label="box"
  AllowCompound = false
  Group = -> [Sketch,Pad,Sketch001,Pocket,Sketch002,Pad001,Sketch003,Pocket001,Sketch010,Pocket004,Mirrored002,Sketch014,Pocket006,Chamfer007,MultiTransform001,LinearPattern003,LinearPattern004,Sketch030,Pad012,Sketch032,Pocket011,Sketch033,Pocket012,Sketch034,Pocket013,Chamfer006,MultiTransform,LinearPattern]
  Origin = -> Origin002
  Tip = -> MultiTransform
FEATURE [App::Part] Part  label="Box"
  Base_BoxWidth = 210
  Group = -> [Body]
  Origin = -> Origin001
FEATURE [Part::FeaturePython] Screw012  label="M3x20-Screw"  # WARN: FeaturePython — macro-defined, semantics opaque (R4)
  Diameter = 3
  Invert = false
  LeftHanded = false
  Length = 4
  LengthCustom = 20
  MatchOuter = false
  OffsetAngle = 0
  Placement = pos=(84.8,90.5014,38) rot=(-1,0,0;1.5708rad)
  Thread = false
  Type = 51
FEATURE [App::FeaturePython] Joint026  label="Fixed026"  # Assembly joint (typed FeaturePython)
  Angle = 0
  AngleMax = 0
  AngleMin = 0
  Detach1 = false
  Detach2 = false
  Distance = 0
  Distance2 = 0
  EnableAngleMax = false
  EnableAngleMin = false
  EnableLengthMax = false
  EnableLengthMin = false
  JointType = 0 (Fixed)
  LengthMax = 0
  LengthMin = 0
  Placement1 = pos=(0,0,-1.90142) rot=(0,0,1;0rad)
  Placement2 = pos=(84.8,88.6,38) rot=(1,0,0;1.5708rad)
  Reference1 = -> Assembly [Screw012.Edge6,Screw012.Edge6]
  Reference2 = -> Assembly [Box.Body.Edge334,Box.Body.Edge334]
  Suppressed = false
FEATURE [Part::FeaturePython] Washer  label="M3-Washer"  # WARN: FeaturePython — macro-defined, semantics opaque (R4)
  Diameter = 4
  Invert = false
  MatchOuter = false
  OffsetAngle = 0
  Placement = pos=(84.8,74.7,38) rot=(0.57735,-0.57735,0.57735;2.0944rad)
  Type = 8
FEATURE [Part::FeaturePython] Nut  label="M3-Nut"  # WARN: FeaturePython — macro-defined, semantics opaque (R4)
  Diameter = 4
  Invert = false
  LeftHanded = false
  MatchOuter = false
  OffsetAngle = 0
  Placement = pos=(84.8,74.2,38) rot=(0.774597,-0.447214,0.447214;1.82348rad)
  Thread = false
  Type = 31
FEATURE [App::FeaturePython] Joint030  label="Fixed030"  # Assembly joint (typed FeaturePython)
  Angle = 0
  AngleMax = 0
  AngleMin = 0
  Detach1 = false
  Detach2 = false
  Distance = 0
  Distance2 = 0
  EnableAngleMax = false
  EnableAngleMin = false
  EnableLengthMax = false
  EnableLengthMin = false
  JointType = 0 (Fixed)
  LengthMax = 0
  LengthMin = 0
  Placement2 = pos=(0,0,1.4) rot=(0,1,0;3.14159rad)
  Reference1 = -> Assembly [Washer.Edge5,Washer.Edge5]
  Reference2 = -> Assembly [NF_A4x10_FLX001.Part__Feature004.Edge4,NF_A4x10_FLX001.Part__Feature004.Edge4]
  Suppressed = false
FEATURE [App::FeaturePython] Joint031  label="Fixed031"  # Assembly joint (typed FeaturePython)
  Angle = 0
  AngleMax = 0
  AngleMin = 0
  Detach1 = false
  Detach2 = false
  Distance = 0
  Distance2 = 0
  EnableAngleMax = false
  EnableAngleMin = false
  EnableLengthMax = false
  EnableLengthMin = false
  JointType = 0 (Fixed)
  LengthMax = 0
  LengthMin = 0
  Offset2 = pos=(0,0,0) rot=(0,0,1;0.523599rad)
  Placement1 = pos=(0,0,0.5) rot=(0,0,1;0rad)
  Placement2 = pos=(0,0,0) rot=(0,0,1;0.523599rad)
  Reference1 = -> Assembly [Washer.Edge1,Washer.Edge1]
  Reference2 = -> Assembly [Nut.Edge27,Nut.Edge27]
  Suppressed = false
FEATURE [Part::FeaturePython] Screw016  label="M3x8-Screw006"  # WARN: FeaturePython — macro-defined, semantics opaque (R4)
  Diameter = 3
  Invert = false
  LeftHanded = false
  Length = 0
  LengthCustom = 8
  MatchOuter = false
  OffsetAngle = 0
  Placement = pos=(-96.15,-72.4,43.8407) rot=(0,0,1;0rad)
  Thread = false
  Type = 51
FEATURE [App::FeaturePython] Joint038  label="Fixed038"  # Assembly joint (typed FeaturePython)
  Angle = 0
  AngleMax = 0
  AngleMin = 0
  Detach1 = false
  Detach2 = false
  Distance = 0
  Distance2 = 0
  EnableAngleMax = false
  EnableAngleMin = false
  EnableLengthMax = false
  EnableLengthMin = false
  JointType = 0 (Fixed)
  LengthMax = 0
  LengthMin = 0
  Placement1 = pos=(-96.025,-71.525,0.01) rot=(0,0,1;0rad)
  Placement2 = pos=(0,0,-1.83071) rot=(0,0,1;0rad)
  Reference1 = -> Assembly [Top_Cover.Body006.Edge37,Top_Cover.Body006.Edge37]
  Reference2 = -> Assembly [Screw016.Edge6,Screw016.Edge6]
  Suppressed = false
FEATURE [Part::FeaturePython] Screw017  label="M3x8-Screw007"  # WARN: FeaturePython — macro-defined, semantics opaque (R4)
  Diameter = 3
  Invert = false
  LeftHanded = false
  Length = 0
  LengthCustom = 8
  MatchOuter = false
  OffsetAngle = 0
  Placement = pos=(95.9,-72.4,43.8407) rot=(0,0,1;0rad)
  Thread = false
  Type = 51
FEATURE [App::FeaturePython] Joint039  label="Fixed039"  # Assembly joint (typed FeaturePython)
  Angle = 0
  AngleMax = 0
  AngleMin = 0
  Detach1 = false
  Detach2 = false
  Distance = 0
  Distance2 = 0
  EnableAngleMax = false
  EnableAngleMin = false
  EnableLengthMax = false
  EnableLengthMin = false
  JointType = 0 (Fixed)
  LengthMax = 0
  LengthMin = 0
  Placement1 = pos=(0,0,-1.83071) rot=(0,0,1;0rad)
  Placement2 = pos=(96.025,-71.525,0.01) rot=(0,0,1;0rad)
  Reference1 = -> Assembly [Screw017.Edge6,Screw017.Edge6]
  Reference2 = -> Assembly [Top_Cover.Body006.Edge41,Top_Cover.Body006.Edge41]
  Suppressed = false
FEATURE [Part::FeaturePython] Screw018  label="M3x8-Screw010"  # WARN: FeaturePython — macro-defined, semantics opaque (R4)
  Diameter = 3
  Invert = false
  LeftHanded = false
  Length = 0
  LengthCustom = 8
  MatchOuter = false
  OffsetAngle = 0
  Placement = pos=(-96.15,81.15,43.8407) rot=(0,0,1;0rad)
  Thread = false
  Type = 51
FEATURE [App::FeaturePython] Joint040  label="Fixed040"  # Assembly joint (typed FeaturePython)
  Angle = 0
  AngleMax = 0
  AngleMin = 0
  Detach1 = false
  Detach2 = false
  Distance = 0
  Distance2 = 0
  EnableAngleMax = false
  EnableAngleMin = false
  EnableLengthMax = false
  EnableLengthMin = false
  JointType = 0 (Fixed)
  LengthMax = 0
  LengthMin = 0
  Placement1 = pos=(0,0,-1.83071) rot=(0,0,1;0rad)
  Placement2 = pos=(-96.025,82.025,0.01) rot=(0,0,1;0rad)
  Reference1 = -> Assembly [Screw018.Edge6,Screw018.Edge6]
  Reference2 = -> Assembly [Top_Cover.Body006.Edge2,Top_Cover.Body006.Edge2]
  Suppressed = false
FEATURE [Part::FeaturePython] Screw019  label="M3x8-Screw011"  # WARN: FeaturePython — macro-defined, semantics opaque (R4)
  Diameter = 3
  Invert = false
  LeftHanded = false
  Length = 0
  LengthCustom = 8
  MatchOuter = false
  OffsetAngle = 0
  Placement = pos=(95.9,81.15,43.8307) rot=(0,0,1;0rad)
  Thread = false
  Type = 51
FEATURE [App::FeaturePython] Joint041  label="Fixed041"  # Assembly joint (typed FeaturePython)
  Angle = 0
  AngleMax = 0
  AngleMin = 0
  Detach1 = false
  Detach2 = false
  Distance = 0
  Distance2 = 0
  EnableAngleMax = false
  EnableAngleMin = false
  EnableLengthMax = false
  EnableLengthMin = false
  JointType = 0 (Fixed)
  LengthMax = 0
  LengthMin = 0
  Placement1 = pos=(0,0,-1.83071) rot=(0,0,1;0rad)
  Placement2 = pos=(96.025,82.025,0) rot=(0,0,1;0rad)
  Reference1 = -> Assembly [Screw019.Edge6,Screw019.Edge6]
  Reference2 = -> Assembly [Top_Cover.Body006.Edge15,Top_Cover.Body006.Edge15]
  Suppressed = false
FEATURE [Assembly::JointGroup] Joints
  Group = -> [GroundedJoint,Joint,Joint001,Joint004,Joint006,Joint007,Joint011,Joint012,Joint013,Joint015,Joint016,Joint017,Joint018,Joint019,Joint021,Joint022,Joint023,Joint024,Joint026,Joint030,Joint031,Joint038,Joint039,Joint040,Joint041]
FEATURE [Assembly::AssemblyObject] Assembly
  Group = -> [Joints,Box,GroundedJoint,Front_cover,Top_Cover,Joint,Joint001,Ear_3D,Ear_3D001,NF_A4x10_FLX001,Joint004,Joint006,Joint007,Screw,Screw004,Joint011,Screw005,Screw006,Screw001,Joint012,Screw002,Joint013,Screw003,Screw007,Screw008,Screw009,Screw010,Screw011,Screw016,Screw017,Screw018,Screw019,Screw012,Washer,Nut,Joint015,Joint016,Joint017,Joint018,Joint019,Joint021,Joint022,Joint023,Joint024,Joint026,+6 more]
  Origin = -> Origin
  Type = Assembly
FEATURE [App::Point] Origin025  label="Origin"
  Role = Origin
FEATURE [App::Point] Origin026  label="Origin"
  Role = Origin
FEATURE [App::Point] Origin027  label="Origin"
  Role = Origin
FEATURE [App::Point] Origin028  label="Origin"
  Role = Origin
FEATURE [App::Point] Origin029  label="Origin"
  Role = Origin
FEATURE [App::Point] Origin030  label="Origin"
  Role = Origin
FEATURE [App::Point] Origin031  label="Origin"
  Role = Origin
FEATURE [App::Point] Origin032  label="Origin"
  Role = Origin
FEATURE [App::Point] Origin033  label="Origin"
  Role = Origin
FEATURE [App::Point] Origin034  label="Origin"
  Role = Origin
FEATURE [App::Point] Origin035  label="Origin"
  Role = Origin
FEATURE [App::Point] Origin036  label="Origin"
  Role = Origin
FEATURE [App::Point] Origin037  label="Origin"
  Role = Origin
FEATURE [App::Point] Origin038  label="Origin"
  Role = Origin
FEATURE [App::Point] Origin039  label="Origin"
  Role = Origin
FEATURE [PartDesign::Fillet] Fillet001
  Base = -> Fillet [Edge21,Edge11]
  BaseFeature = -> Fillet
  Placement = pos=(0,0,0) rot=(1,1,1;2.0944rad)
  Radius = 6.2
  Refine = true
  SupportTransform = false
  Suppressed = false
  UseAllEdges = false
FEATURE [PartDesign::Body] Body004  label="3DEar"
  AllowCompound = false
  Group = -> [Sketch011,Pad006,Chamfer003,Sketch012,Pad007,Sketch013,Pocket005,Fillet,Fillet001]
  Origin = -> Origin011
  Tip = -> Fillet001
FEATURE [App::Part] Part005  label="Ear 3D"
  Group = -> [Body004]
  Origin = -> Origin013
  Placement = pos=(0,-2.84e-14,0) rot=(0,0,1;0rad)
